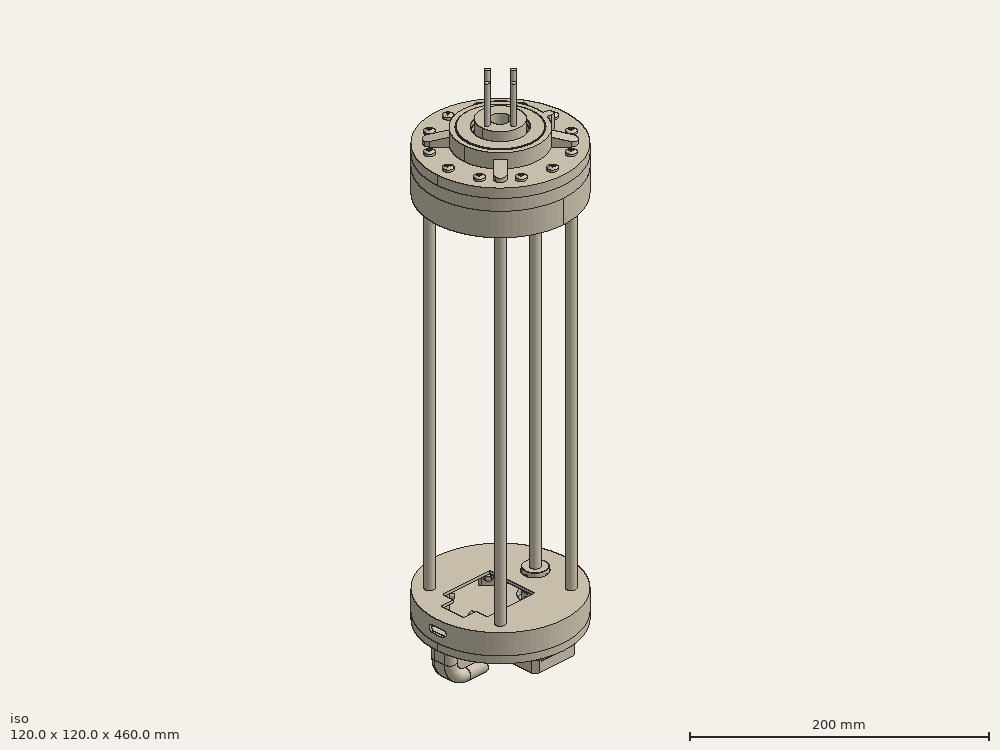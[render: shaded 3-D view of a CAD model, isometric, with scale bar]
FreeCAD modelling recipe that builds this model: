
FCSTD DOCUMENT  (FreeCAD 0.19R)
Label: Z-axis_a2p
License: All rights reserved
LicenseURL: http://en.wikipedia.org/wiki/All_rights_reserved
objects: Part::FeaturePython×103, App::FeaturePython×86, Spreadsheet::Sheet×2
note: 103 computed .brp shape members not serialized (recipe doc carries the construction recipe); baked Part::Feature solids carry a one-line shape summary decoded from their .brp

FEATURE [Part::FeaturePython] b_Z_axis_top_plate_001_  label="Z-axis_top_plate_001"  # a2plus imported part (geometry in sourceFile) (typed FeaturePython)
  a2p_Version = V0.1
  fixedPosition = true
  objectType = a2pPart
  sourceFile = ./Z-axis_top_plate.FCStd
  subassemblyImport = false
  timeLastImport = 1619853054
  updateColors = true
FEATURE [Part::FeaturePython] b_Clamp_smoth_rod_8mm_single_screw_001_  label="Clamp_smoth_rod_8mm_single_screw_001"  # a2plus imported part (geometry in sourceFile) (typed FeaturePython)
  Placement = pos=(-33.5876,-33.5876,13) rot=(0,0,1;0.785398rad)
  a2p_Version = V0.1
  fixedPosition = false
  objectType = a2pPart
  sourceFile = ./Clamp_smoth_rod_8mm_single_screw.FCStd
  subassemblyImport = false
  timeLastImport = 1.61989e+09
  updateColors = true
FEATURE [Part::FeaturePython] b_Clamp_smoth_rod_8mm_single_screw_001_001  label="Clamp_smoth_rod_8mm_single_screw_002"  # a2plus imported part (geometry in sourceFile) (typed FeaturePython)
  Placement = pos=(33.5876,33.5876,13) rot=(0,0,1;3.92699rad)
  a2p_Version = V0.1
  fixedPosition = false
  objectType = a2pPart
  sourceFile = ./Clamp_smoth_rod_8mm_single_screw.FCStd
  subassemblyImport = false
  timeLastImport = 1.61989e+09
  updateColors = true
FEATURE [Part::FeaturePython] b_Top_cover_8mm_001_  label="Top_cover_8mm_001"  # a2plus imported part (geometry in sourceFile) (typed FeaturePython)
  Placement = pos=(-1.16153e-07,1.92173e-07,24) rot=(0.707107,0.707107,0;3.14159rad)
  a2p_Version = V0.1
  fixedPosition = false
  objectType = a2pPart
  sourceFile = ./Top_cover_8mm.FCStd
  subassemblyImport = false
  timeLastImport = 1.62017e+09
  updateColors = true
FEATURE [App::FeaturePython] planeCoincident_003  label="planeCoincident_003__Z-axis_top_plate_001"  # a2plus constraint (typed FeaturePython)
  Object1 = b_Top_cover_8mm_001_
  Object2 = b_Z_axis_top_plate_001_
  ParentTreeObject = -> b_Top_cover_8mm_001_
  SubElement1 = Face11
  SubElement2 = Face1
  Suppressed = false
  Type = plane
  directionConstraint = 1
  offset = 0
FEATURE [App::FeaturePython] planeCoincident_003_mirror  label="planeCoincident_003__Top_cover_8mm_001"  # a2plus constraint (typed FeaturePython)
  Object1 = b_Top_cover_8mm_001_
  Object2 = b_Z_axis_top_plate_001_
  ParentTreeObject = -> b_Z_axis_top_plate_001_
  SubElement1 = Face11
  SubElement2 = Face1
  Suppressed = false
  Type = plane
  directionConstraint = 1
  offset = 0
FEATURE [App::FeaturePython] axisCoincident_005  label="axisCoincident_005__Z-axis_top_plate_001"  # a2plus constraint (typed FeaturePython)
  Object1 = b_Top_cover_8mm_001_
  Object2 = b_Z_axis_top_plate_001_
  ParentTreeObject = -> b_Top_cover_8mm_001_
  SubElement1 = Face16
  SubElement2 = Face11
  Suppressed = false
  Type = axial
  directionConstraint = 1
  lockRotation = false
FEATURE [App::FeaturePython] axisCoincident_005_mirror  label="axisCoincident_005__Top_cover_8mm_001"  # a2plus constraint (typed FeaturePython)
  Object1 = b_Top_cover_8mm_001_
  Object2 = b_Z_axis_top_plate_001_
  ParentTreeObject = -> b_Z_axis_top_plate_001_
  SubElement1 = Face16
  SubElement2 = Face11
  Suppressed = false
  Type = axial
  directionConstraint = 1
  lockRotation = false
FEATURE [App::FeaturePython] axisCoincident_001  label="axisCoincident_001__Z-axis_top_plate_001"  # a2plus constraint (typed FeaturePython)
  Object1 = b_Clamp_smoth_rod_8mm_single_screw_001_
  Object2 = b_Z_axis_top_plate_001_
  ParentTreeObject = -> b_Clamp_smoth_rod_8mm_single_screw_001_
  SubElement1 = Face67
  SubElement2 = Face29
  Suppressed = false
  Type = axial
  directionConstraint = 0
  lockRotation = false
FEATURE [App::FeaturePython] axisCoincident_001_mirror  label="axisCoincident_001__Clamp_smoth_rod_8mm_single_screw_001"  # a2plus constraint (typed FeaturePython)
  Object1 = b_Clamp_smoth_rod_8mm_single_screw_001_
  Object2 = b_Z_axis_top_plate_001_
  ParentTreeObject = -> b_Z_axis_top_plate_001_
  SubElement1 = Face67
  SubElement2 = Face29
  Suppressed = false
  Type = axial
  directionConstraint = 0
  lockRotation = false
FEATURE [App::FeaturePython] axisCoincident_002  label="axisCoincident_002__Clamp_smoth_rod_8mm_single_screw_001"  # a2plus constraint (typed FeaturePython)
  Object1 = b_Z_axis_top_plate_001_
  Object2 = b_Clamp_smoth_rod_8mm_single_screw_001_
  ParentTreeObject = -> b_Z_axis_top_plate_001_
  SubElement1 = Face31
  SubElement2 = Face66
  Suppressed = false
  Type = axial
  directionConstraint = 0
  lockRotation = false
FEATURE [App::FeaturePython] axisCoincident_002_mirror  label="axisCoincident_002__Z-axis_top_plate_001"  # a2plus constraint (typed FeaturePython)
  Object1 = b_Z_axis_top_plate_001_
  Object2 = b_Clamp_smoth_rod_8mm_single_screw_001_
  ParentTreeObject = -> b_Clamp_smoth_rod_8mm_single_screw_001_
  SubElement1 = Face31
  SubElement2 = Face66
  Suppressed = false
  Type = axial
  directionConstraint = 0
  lockRotation = false
FEATURE [App::FeaturePython] axisCoincident_003  label="axisCoincident_003__Clamp_smoth_rod_8mm_single_screw_002"  # a2plus constraint (typed FeaturePython)
  Object1 = b_Z_axis_top_plate_001_
  Object2 = b_Clamp_smoth_rod_8mm_single_screw_001_001
  ParentTreeObject = -> b_Z_axis_top_plate_001_
  SubElement1 = Face21
  SubElement2 = Face67
  Suppressed = false
  Type = axial
  directionConstraint = 0
  lockRotation = false
FEATURE [App::FeaturePython] axisCoincident_003_mirror  label="axisCoincident_003__Z-axis_top_plate_001"  # a2plus constraint (typed FeaturePython)
  Object1 = b_Z_axis_top_plate_001_
  Object2 = b_Clamp_smoth_rod_8mm_single_screw_001_001
  ParentTreeObject = -> b_Clamp_smoth_rod_8mm_single_screw_001_001
  SubElement1 = Face21
  SubElement2 = Face67
  Suppressed = false
  Type = axial
  directionConstraint = 0
  lockRotation = false
FEATURE [App::FeaturePython] axisCoincident_004  label="axisCoincident_004__Z-axis_top_plate_001"  # a2plus constraint (typed FeaturePython)
  Object1 = b_Clamp_smoth_rod_8mm_single_screw_001_001
  Object2 = b_Z_axis_top_plate_001_
  ParentTreeObject = -> b_Clamp_smoth_rod_8mm_single_screw_001_001
  SubElement1 = Face66
  SubElement2 = Face23
  Suppressed = false
  Type = axial
  directionConstraint = 0
  lockRotation = false
FEATURE [App::FeaturePython] axisCoincident_004_mirror  label="axisCoincident_004__Clamp_smoth_rod_8mm_single_screw_002"  # a2plus constraint (typed FeaturePython)
  Object1 = b_Clamp_smoth_rod_8mm_single_screw_001_001
  Object2 = b_Z_axis_top_plate_001_
  ParentTreeObject = -> b_Z_axis_top_plate_001_
  SubElement1 = Face66
  SubElement2 = Face23
  Suppressed = false
  Type = axial
  directionConstraint = 0
  lockRotation = false
FEATURE [Part::FeaturePython] b_Clamp_smoth_rod_8mm_single_screw_001_002  label="Clamp_smoth_rod_8mm_single_screw_003"  # a2plus imported part (geometry in sourceFile) (typed FeaturePython)
  Placement = pos=(33.5876,-33.5876,13) rot=(0.382683,0.92388,0;3.14159rad)
  a2p_Version = V0.1
  fixedPosition = false
  objectType = a2pPart
  sourceFile = ./Clamp_smoth_rod_8mm_single_screw.FCStd
  subassemblyImport = false
  timeLastImport = 1.61989e+09
  updateColors = true
FEATURE [Part::FeaturePython] b_Clamp_smoth_rod_8mm_single_screw_001_003  label="Clamp_smoth_rod_8mm_single_screw_004"  # a2plus imported part (geometry in sourceFile) (typed FeaturePython)
  Placement = pos=(-33.5876,33.5876,13) rot=(0.92388,-0.382683,0;3.14159rad)
  a2p_Version = V0.1
  fixedPosition = false
  objectType = a2pPart
  sourceFile = ./Clamp_smoth_rod_8mm_single_screw.FCStd
  subassemblyImport = false
  timeLastImport = 1.61989e+09
  updateColors = true
FEATURE [App::FeaturePython] planeCoincident_001  label="planeCoincident_001__Z-axis_top_plate_001"  # a2plus constraint (typed FeaturePython)
  Object1 = b_Clamp_smoth_rod_8mm_single_screw_001_003
  Object2 = b_Z_axis_top_plate_001_
  ParentTreeObject = -> b_Clamp_smoth_rod_8mm_single_screw_001_003
  SubElement1 = Face36
  SubElement2 = Face1
  Suppressed = false
  Type = plane
  directionConstraint = 1
  offset = 0
FEATURE [App::FeaturePython] planeCoincident_001_mirror  label="planeCoincident_001__Clamp_smoth_rod_8mm_single_screw_004"  # a2plus constraint (typed FeaturePython)
  Object1 = b_Clamp_smoth_rod_8mm_single_screw_001_003
  Object2 = b_Z_axis_top_plate_001_
  ParentTreeObject = -> b_Z_axis_top_plate_001_
  SubElement1 = Face36
  SubElement2 = Face1
  Suppressed = false
  Type = plane
  directionConstraint = 1
  offset = 0
FEATURE [App::FeaturePython] axisCoincident_007  label="axisCoincident_007__Z-axis_top_plate_001"  # a2plus constraint (typed FeaturePython)
  Object1 = b_Clamp_smoth_rod_8mm_single_screw_001_003
  Object2 = b_Z_axis_top_plate_001_
  ParentTreeObject = -> b_Clamp_smoth_rod_8mm_single_screw_001_003
  SubElement1 = Face67
  SubElement2 = Face27
  Suppressed = false
  Type = axial
  directionConstraint = 1
  lockRotation = false
FEATURE [App::FeaturePython] axisCoincident_007_mirror  label="axisCoincident_007__Clamp_smoth_rod_8mm_single_screw_004"  # a2plus constraint (typed FeaturePython)
  Object1 = b_Clamp_smoth_rod_8mm_single_screw_001_003
  Object2 = b_Z_axis_top_plate_001_
  ParentTreeObject = -> b_Z_axis_top_plate_001_
  SubElement1 = Face67
  SubElement2 = Face27
  Suppressed = false
  Type = axial
  directionConstraint = 1
  lockRotation = false
FEATURE [App::FeaturePython] axisCoincident_008  label="axisCoincident_008__Z-axis_top_plate_001"  # a2plus constraint (typed FeaturePython)
  Object1 = b_Clamp_smoth_rod_8mm_single_screw_001_003
  Object2 = b_Z_axis_top_plate_001_
  ParentTreeObject = -> b_Clamp_smoth_rod_8mm_single_screw_001_003
  SubElement1 = Face66
  SubElement2 = Face25
  Suppressed = false
  Type = axial
  directionConstraint = 1
  lockRotation = false
FEATURE [App::FeaturePython] axisCoincident_008_mirror  label="axisCoincident_008__Clamp_smoth_rod_8mm_single_screw_004"  # a2plus constraint (typed FeaturePython)
  Object1 = b_Clamp_smoth_rod_8mm_single_screw_001_003
  Object2 = b_Z_axis_top_plate_001_
  ParentTreeObject = -> b_Z_axis_top_plate_001_
  SubElement1 = Face66
  SubElement2 = Face25
  Suppressed = false
  Type = axial
  directionConstraint = 1
  lockRotation = false
FEATURE [App::FeaturePython] planeCoincident_002  label="planeCoincident_002__Clamp_smoth_rod_8mm_single_screw_003"  # a2plus constraint (typed FeaturePython)
  Object1 = b_Z_axis_top_plate_001_
  Object2 = b_Clamp_smoth_rod_8mm_single_screw_001_002
  ParentTreeObject = -> b_Z_axis_top_plate_001_
  SubElement1 = Face1
  SubElement2 = Face36
  Suppressed = false
  Type = plane
  directionConstraint = 1
  offset = 0
FEATURE [App::FeaturePython] planeCoincident_002_mirror  label="planeCoincident_002__Z-axis_top_plate_001"  # a2plus constraint (typed FeaturePython)
  Object1 = b_Z_axis_top_plate_001_
  Object2 = b_Clamp_smoth_rod_8mm_single_screw_001_002
  ParentTreeObject = -> b_Clamp_smoth_rod_8mm_single_screw_001_002
  SubElement1 = Face1
  SubElement2 = Face36
  Suppressed = false
  Type = plane
  directionConstraint = 1
  offset = 0
FEATURE [App::FeaturePython] axisCoincident_009  label="axisCoincident_009__Z-axis_top_plate_001"  # a2plus constraint (typed FeaturePython)
  Object1 = b_Clamp_smoth_rod_8mm_single_screw_001_002
  Object2 = b_Z_axis_top_plate_001_
  ParentTreeObject = -> b_Clamp_smoth_rod_8mm_single_screw_001_002
  SubElement1 = Face67
  SubElement2 = Face19
  Suppressed = false
  Type = axial
  directionConstraint = 1
  lockRotation = false
FEATURE [App::FeaturePython] axisCoincident_009_mirror  label="axisCoincident_009__Clamp_smoth_rod_8mm_single_screw_003"  # a2plus constraint (typed FeaturePython)
  Object1 = b_Clamp_smoth_rod_8mm_single_screw_001_002
  Object2 = b_Z_axis_top_plate_001_
  ParentTreeObject = -> b_Z_axis_top_plate_001_
  SubElement1 = Face67
  SubElement2 = Face19
  Suppressed = false
  Type = axial
  directionConstraint = 1
  lockRotation = false
FEATURE [App::FeaturePython] axisCoincident_010  label="axisCoincident_010__Z-axis_top_plate_001"  # a2plus constraint (typed FeaturePython)
  Object1 = b_Clamp_smoth_rod_8mm_single_screw_001_002
  Object2 = b_Z_axis_top_plate_001_
  ParentTreeObject = -> b_Clamp_smoth_rod_8mm_single_screw_001_002
  SubElement1 = Face66
  SubElement2 = Face33
  Suppressed = false
  Type = axial
  directionConstraint = 1
  lockRotation = false
FEATURE [App::FeaturePython] axisCoincident_010_mirror  label="axisCoincident_010__Clamp_smoth_rod_8mm_single_screw_003"  # a2plus constraint (typed FeaturePython)
  Object1 = b_Clamp_smoth_rod_8mm_single_screw_001_002
  Object2 = b_Z_axis_top_plate_001_
  ParentTreeObject = -> b_Z_axis_top_plate_001_
  SubElement1 = Face66
  SubElement2 = Face33
  Suppressed = false
  Type = axial
  directionConstraint = 1
  lockRotation = false
FEATURE [Part::FeaturePython] b_Z_axis_endstop_support_001_  label="Z-axis_endstop_support_001"  # a2plus imported part (geometry in sourceFile) (typed FeaturePython)
  Placement = pos=(-53,1.64821e-06,1.13151e-07) rot=(1,0,0;3.14159rad)
  a2p_Version = V0.1
  fixedPosition = false
  objectType = a2pPart
  sourceFile = ./Z-axis_endstop_support.FCStd
  subassemblyImport = false
  timeLastImport = 1.61989e+09
  updateColors = true
FEATURE [App::FeaturePython] planeCoincident_004  label="planeCoincident_004__Z-axis_top_plate_001"  # a2plus constraint (typed FeaturePython)
  Object1 = b_Z_axis_endstop_support_001_
  Object2 = b_Z_axis_top_plate_001_
  ParentTreeObject = -> b_Z_axis_endstop_support_001_
  SubElement1 = Face1
  SubElement2 = Face48
  Suppressed = false
  Type = plane
  directionConstraint = 0
  offset = 0
FEATURE [App::FeaturePython] planeCoincident_004_mirror  label="planeCoincident_004__Z-axis_endstop_support_001"  # a2plus constraint (typed FeaturePython)
  Object1 = b_Z_axis_endstop_support_001_
  Object2 = b_Z_axis_top_plate_001_
  ParentTreeObject = -> b_Z_axis_top_plate_001_
  SubElement1 = Face1
  SubElement2 = Face48
  Suppressed = false
  Type = plane
  directionConstraint = 0
  offset = 0
FEATURE [App::FeaturePython] axisCoincident_011  label="axisCoincident_011__Z-axis_top_plate_001"  # a2plus constraint (typed FeaturePython)
  Object1 = b_Z_axis_endstop_support_001_
  Object2 = b_Z_axis_top_plate_001_
  ParentTreeObject = -> b_Z_axis_endstop_support_001_
  SubElement1 = Face74
  SubElement2 = Face49
  Suppressed = false
  Type = axial
  directionConstraint = 1
  lockRotation = true
FEATURE [App::FeaturePython] axisCoincident_011_mirror  label="axisCoincident_011__Z-axis_endstop_support_001"  # a2plus constraint (typed FeaturePython)
  Object1 = b_Z_axis_endstop_support_001_
  Object2 = b_Z_axis_top_plate_001_
  ParentTreeObject = -> b_Z_axis_top_plate_001_
  SubElement1 = Face74
  SubElement2 = Face49
  Suppressed = false
  Type = axial
  directionConstraint = 1
  lockRotation = true
FEATURE [Part::FeaturePython] b_Stepper_NEMA_17____20mm_shaft1_001_  label="Stepper NEMA 17 -  20mm shaft1_001"  # a2plus imported part (geometry in sourceFile) (typed FeaturePython)
  Placement = pos=(24.5386,-37.2291,-61.0261) rot=(0,0,1;0rad)
  a2p_Version = V0.1
  fixedPosition = false
  muxInfo = <blob: 18848 chars omitted>
  objectType = a2pPart
  sourceFile = ./Stepper NEMA 17 -  20mm shaft.step
  subassemblyImport = false
  timeLastImport = 1598802185
  updateColors = true
FEATURE [App::FeaturePython] circularEdge_001  label="circularEdge_001__Z-axis_top_plate_001"  # a2plus constraint (typed FeaturePython)
  Object1 = b_Stepper_NEMA_17____20mm_shaft1_001_
  Object2 = b_Z_axis_top_plate_001_
  ParentTreeObject = -> b_Stepper_NEMA_17____20mm_shaft1_001_
  SubElement1 = Edge25
  SubElement2 = Edge132
  Suppressed = false
  Type = circularEdge
  directionConstraint = 0
  lockRotation = true
  offset = 0
FEATURE [App::FeaturePython] circularEdge_001_mirror  label="circularEdge_001__Stepper NEMA 17 -  20mm shaft1_001"  # a2plus constraint (typed FeaturePython)
  Object1 = b_Stepper_NEMA_17____20mm_shaft1_001_
  Object2 = b_Z_axis_top_plate_001_
  ParentTreeObject = -> b_Z_axis_top_plate_001_
  SubElement1 = Edge25
  SubElement2 = Edge132
  Suppressed = false
  Type = circularEdge
  directionConstraint = 0
  lockRotation = true
  offset = 0
FEATURE [Part::FeaturePython] b_Micro_switch1_001_  label="Micro switch1_001"  # a2plus imported part (geometry in sourceFile) (typed FeaturePython)
  Placement = pos=(-35.8,3,0.6) rot=(1,0,0;1.5708rad)
  a2p_Version = V0.1
  fixedPosition = false
  muxInfo = <blob: 6853 chars omitted>
  objectType = a2pPart
  sourceFile = ./Micro switch.step
  subassemblyImport = false
  timeLastImport = 1598970250
  updateColors = true
FEATURE [Part::FeaturePython] b_pin_3mmx10mm_001_  label="pin_3mmx10mm_001"  # a2plus imported part (geometry in sourceFile) (typed FeaturePython)
  Placement = pos=(-30.8,1.00232e-07,-1.9) rot=(0.18533,0,-0.982676;0rad)
  a2p_Version = V0.1
  fixedPosition = false
  muxInfo = [VERTEXES] | V;Pad;1;2; | V;Pad;2;2; | [EDGES] | E;Pad;1;3; | E;Pad;2;3; | E;Pad;3;3; | [FACES] | F;Pad;1;3; | F;Pad;2;3; | F;Pad;3;3;
  objectType = a2pPart
  sourceFile = ./pin_3mmx10mm.FCStd
  subassemblyImport = false
  timeLastImport = 1.61984e+09
  updateColors = true
FEATURE [App::FeaturePython] axisCoincident_012  label="axisCoincident_012__pin_3mmx10mm_001"  # a2plus constraint (typed FeaturePython)
  Object1 = b_Micro_switch1_001_
  Object2 = b_pin_3mmx10mm_001_
  ParentTreeObject = -> b_Micro_switch1_001_
  SubElement1 = Face10
  SubElement2 = Face1
  Suppressed = false
  Type = axial
  directionConstraint = 1
  lockRotation = false
FEATURE [App::FeaturePython] axisCoincident_012_mirror  label="axisCoincident_012__Micro switch1_001"  # a2plus constraint (typed FeaturePython)
  Object1 = b_Micro_switch1_001_
  Object2 = b_pin_3mmx10mm_001_
  ParentTreeObject = -> b_pin_3mmx10mm_001_
  SubElement1 = Face10
  SubElement2 = Face1
  Suppressed = false
  Type = axial
  directionConstraint = 1
  lockRotation = false
FEATURE [App::FeaturePython] planeCoincident_005  label="planeCoincident_005__Micro switch1_001"  # a2plus constraint (typed FeaturePython)
  Object1 = b_pin_3mmx10mm_001_
  Object2 = b_Micro_switch1_001_
  ParentTreeObject = -> b_pin_3mmx10mm_001_
  SubElement1 = Face3
  SubElement2 = Face8
  Suppressed = false
  Type = plane
  directionConstraint = 1
  offset = 2
FEATURE [App::FeaturePython] planeCoincident_005_mirror  label="planeCoincident_005__pin_3mmx10mm_001"  # a2plus constraint (typed FeaturePython)
  Object1 = b_pin_3mmx10mm_001_
  Object2 = b_Micro_switch1_001_
  ParentTreeObject = -> b_Micro_switch1_001_
  SubElement1 = Face3
  SubElement2 = Face8
  Suppressed = false
  Type = plane
  directionConstraint = 1
  offset = 2
FEATURE [App::FeaturePython] axisCoincident_013  label="axisCoincident_013__pin_3mmx10mm_001"  # a2plus constraint (typed FeaturePython)
  Object1 = b_Z_axis_endstop_support_001_
  Object2 = b_pin_3mmx10mm_001_
  ParentTreeObject = -> b_Z_axis_endstop_support_001_
  SubElement1 = Face57
  SubElement2 = Face1
  Suppressed = false
  Type = axial
  directionConstraint = 0
  lockRotation = false
FEATURE [App::FeaturePython] axisCoincident_013_mirror  label="axisCoincident_013__Z-axis_endstop_support_001"  # a2plus constraint (typed FeaturePython)
  Object1 = b_Z_axis_endstop_support_001_
  Object2 = b_pin_3mmx10mm_001_
  ParentTreeObject = -> b_pin_3mmx10mm_001_
  SubElement1 = Face57
  SubElement2 = Face1
  Suppressed = false
  Type = axial
  directionConstraint = 0
  lockRotation = false
FEATURE [App::FeaturePython] planeCoincident_006  label="planeCoincident_006__Z-axis_endstop_support_001"  # a2plus constraint (typed FeaturePython)
  Object1 = b_pin_3mmx10mm_001_
  Object2 = b_Z_axis_endstop_support_001_
  ParentTreeObject = -> b_pin_3mmx10mm_001_
  SubElement1 = Face3
  SubElement2 = Face73
  Suppressed = false
  Type = plane
  directionConstraint = 1
  offset = 0
FEATURE [App::FeaturePython] planeCoincident_006_mirror  label="planeCoincident_006__pin_3mmx10mm_001"  # a2plus constraint (typed FeaturePython)
  Object1 = b_pin_3mmx10mm_001_
  Object2 = b_Z_axis_endstop_support_001_
  ParentTreeObject = -> b_Z_axis_endstop_support_001_
  SubElement1 = Face3
  SubElement2 = Face73
  Suppressed = false
  Type = plane
  directionConstraint = 1
  offset = 0
FEATURE [Part::FeaturePython] b_pin_3mmx10mm_001_001  label="pin_3mmx10mm_002"  # a2plus imported part (geometry in sourceFile) (typed FeaturePython)
  Placement = pos=(-40.3,7.4028e-07,-1.9) rot=(0.15264,0,-0.988282;0rad)
  a2p_Version = V0.1
  fixedPosition = false
  muxInfo = [VERTEXES] | V;Pad;1;2; | V;Pad;2;2; | [EDGES] | E;Pad;1;3; | E;Pad;2;3; | E;Pad;3;3; | [FACES] | F;Pad;1;3; | F;Pad;2;3; | F;Pad;3;3;
  objectType = a2pPart
  sourceFile = ./pin_3mmx10mm.FCStd
  subassemblyImport = false
  timeLastImport = 1.61984e+09
  updateColors = true
FEATURE [App::FeaturePython] axisCoincident_014  label="axisCoincident_014__pin_3mmx10mm_002"  # a2plus constraint (typed FeaturePython)
  Object1 = b_Micro_switch1_001_
  Object2 = b_pin_3mmx10mm_001_001
  ParentTreeObject = -> b_Micro_switch1_001_
  SubElement1 = Face9
  SubElement2 = Face1
  Suppressed = false
  Type = axial
  directionConstraint = 1
  lockRotation = false
FEATURE [App::FeaturePython] axisCoincident_014_mirror  label="axisCoincident_014__Micro switch1_001"  # a2plus constraint (typed FeaturePython)
  Object1 = b_Micro_switch1_001_
  Object2 = b_pin_3mmx10mm_001_001
  ParentTreeObject = -> b_pin_3mmx10mm_001_001
  SubElement1 = Face9
  SubElement2 = Face1
  Suppressed = false
  Type = axial
  directionConstraint = 1
  lockRotation = false
FEATURE [App::FeaturePython] planeCoincident_007  label="planeCoincident_007__pin_3mmx10mm_001"  # a2plus constraint (typed FeaturePython)
  Object1 = b_pin_3mmx10mm_001_001
  Object2 = b_pin_3mmx10mm_001_
  ParentTreeObject = -> b_pin_3mmx10mm_001_001
  SubElement1 = Face3
  SubElement2 = Face3
  Suppressed = false
  Type = plane
  directionConstraint = 0
  offset = 0
FEATURE [App::FeaturePython] planeCoincident_007_mirror  label="planeCoincident_007__pin_3mmx10mm_002"  # a2plus constraint (typed FeaturePython)
  Object1 = b_pin_3mmx10mm_001_001
  Object2 = b_pin_3mmx10mm_001_
  ParentTreeObject = -> b_pin_3mmx10mm_001_
  SubElement1 = Face3
  SubElement2 = Face3
  Suppressed = false
  Type = plane
  directionConstraint = 0
  offset = 0
FEATURE [Part::FeaturePython] b_TR8_lead_screw_300mm_001_  label="TR8_lead_screw_300mm_001"  # a2plus imported part (geometry in sourceFile) (typed FeaturePython)
  Placement = pos=(33,1.0072e-08,20) rot=(0.000129,-0.000114,1;9.8e-05rad)
  a2p_Version = V0.1
  fixedPosition = false
  muxInfo = [VERTEXES] | V;Pad;1;2; | V;Pad;2;2; | [EDGES] | E;Pad;1;3; | E;Pad;2;3; | E;Pad;3;3; | [FACES] | F;Pad;1;3; | F;Pad;2;3; | F;Pad;3;3;
  objectType = a2pPart
  sourceFile = ./TR8_lead_screw_300mm.FCStd
  subassemblyImport = false
  timeLastImport = 1.61984e+09
  updateColors = true
FEATURE [App::FeaturePython] circularEdge_002  label="circularEdge_002__Stepper NEMA 17 -  20mm shaft1_001"  # a2plus constraint (typed FeaturePython)
  Object1 = b_TR8_lead_screw_300mm_001_
  Object2 = b_Stepper_NEMA_17____20mm_shaft1_001_
  ParentTreeObject = -> b_TR8_lead_screw_300mm_001_
  SubElement1 = Edge2
  SubElement2 = Edge23
  Suppressed = false
  Type = circularEdge
  directionConstraint = 0
  lockRotation = false
  offset = 0
FEATURE [App::FeaturePython] circularEdge_002_mirror  label="circularEdge_002__TR8_lead_screw_300mm_001"  # a2plus constraint (typed FeaturePython)
  Object1 = b_TR8_lead_screw_300mm_001_
  Object2 = b_Stepper_NEMA_17____20mm_shaft1_001_
  ParentTreeObject = -> b_Stepper_NEMA_17____20mm_shaft1_001_
  SubElement1 = Edge2
  SubElement2 = Edge23
  Suppressed = false
  Type = circularEdge
  directionConstraint = 0
  lockRotation = false
  offset = 0
FEATURE [Part::FeaturePython] b_Z_axis_bottom_plate_001_  label="Z-axis_bottom_plate_001"  # a2plus imported part (geometry in sourceFile) (typed FeaturePython)
  Placement = pos=(2.49245e-05,-2.45911e-05,360) rot=(1,0,0;3.14159rad)
  a2p_Version = V0.1
  fixedPosition = false
  objectType = a2pPart
  sourceFile = ./Z-axis_bottom_plate.FCStd
  subassemblyImport = false
  timeLastImport = 1.62009e+09
  updateColors = true
FEATURE [Part::FeaturePython] b_Bearing_608_spacer_001_  label="Bearing_608_spacer_001"  # a2plus imported part (geometry in sourceFile) (typed FeaturePython)
  Placement = pos=(33,5.21436e-06,350) rot=(0.866026,-0.5,0;3.14159rad)
  a2p_Version = V0.1
  fixedPosition = false
  objectType = a2pPart
  sourceFile = ./Bearing_608_spacer.FCStd
  subassemblyImport = false
  timeLastImport = 1.61989e+09
  updateColors = true
FEATURE [Part::FeaturePython] b_Ball_bearing_6081_001_  label="Ball_bearing_6081_001"  # a2plus imported part (geometry in sourceFile) (typed FeaturePython)
  Placement = pos=(33,5.96645e-06,310.01) rot=(1,0,0;1.5708rad)
  a2p_Version = V0.1
  fixedPosition = false
  muxInfo = <blob: 2406 chars omitted>
  objectType = a2pPart
  sourceFile = ./Ball_bearing_608.step
  subassemblyImport = false
  timeLastImport = 1.61984e+09
  updateColors = true
FEATURE [Part::FeaturePython] b_J1_coupler_8mm1_001_  label="J1_coupler_8mm1_001"  # a2plus imported part (geometry in sourceFile) (typed FeaturePython)
  Placement = pos=(2.49949e-05,-2.50329e-05,368) rot=(0.57735,0.57735,-0.57735;4.18879rad)
  a2p_Version = V0.1
  fixedPosition = false
  muxInfo = <blob: 10829 chars omitted>
  objectType = a2pPart
  sourceFile = ./J1_coupler_8mm.step
  subassemblyImport = false
  timeLastImport = 1.61984e+09
  updateColors = true
FEATURE [Part::FeaturePython] b_Clamp_smoth_rod_8mm_single_screw_001_004  label="Clamp_smoth_rod_8mm_single_screw_005"  # a2plus imported part (geometry in sourceFile) (typed FeaturePython)
  Placement = pos=(33.5876,33.5876,343) rot=(0,0,1;3.92699rad)
  a2p_Version = V0.1
  fixedPosition = false
  objectType = a2pPart
  sourceFile = ./Clamp_smoth_rod_8mm_single_screw.FCStd
  subassemblyImport = false
  timeLastImport = 1.61989e+09
  updateColors = true
FEATURE [Part::FeaturePython] b_Clamp_smoth_rod_8mm_single_screw_001_005  label="Clamp_smoth_rod_8mm_single_screw_006"  # a2plus imported part (geometry in sourceFile) (typed FeaturePython)
  Placement = pos=(33.5876,-33.5876,343) rot=(0.382683,0.92388,0;3.14159rad)
  a2p_Version = V0.1
  fixedPosition = false
  objectType = a2pPart
  sourceFile = ./Clamp_smoth_rod_8mm_single_screw.FCStd
  subassemblyImport = false
  timeLastImport = 1.61989e+09
  updateColors = true
FEATURE [Part::FeaturePython] b_Clamp_smoth_rod_8mm_single_screw_001_006  label="Clamp_smoth_rod_8mm_single_screw_007"  # a2plus imported part (geometry in sourceFile) (typed FeaturePython)
  Placement = pos=(-33.5875,-33.5876,343) rot=(0,0,1;0.785398rad)
  a2p_Version = V0.1
  fixedPosition = false
  objectType = a2pPart
  sourceFile = ./Clamp_smoth_rod_8mm_single_screw.FCStd
  subassemblyImport = false
  timeLastImport = 1.61989e+09
  updateColors = true
FEATURE [Part::FeaturePython] b_Clamp_smoth_rod_8mm_single_screw_001_007  label="Clamp_smoth_rod_8mm_single_screw_008"  # a2plus imported part (geometry in sourceFile) (typed FeaturePython)
  Placement = pos=(-33.5876,33.5875,343) rot=(0.92388,-0.382683,0;3.14159rad)
  a2p_Version = V0.1
  fixedPosition = false
  objectType = a2pPart
  sourceFile = ./Clamp_smoth_rod_8mm_single_screw.FCStd
  subassemblyImport = false
  timeLastImport = 1.61989e+09
  updateColors = true
FEATURE [Part::FeaturePython] b_Base_cover_8mm_001_  label="Base_cover_8mm_001"  # a2plus imported part (geometry in sourceFile) (typed FeaturePython)
  Placement = pos=(2.46476e-05,-2.35668e-05,329.5) rot=(1,0,0;1.5708rad)
  a2p_Version = V0.1
  fixedPosition = false
  objectType = a2pPart
  sourceFile = ./Base_cover_8mm.FCStd
  subassemblyImport = false
  timeLastImport = 1.61989e+09
  updateColors = true
FEATURE [App::FeaturePython] circularEdge_007  label="circularEdge_007__Bearing_608_spacer_001"  # a2plus constraint (typed FeaturePython)
  Object1 = b_Ball_bearing_6081_001_
  Object2 = b_Bearing_608_spacer_001_
  ParentTreeObject = -> b_Ball_bearing_6081_001_
  SubElement1 = Edge13
  SubElement2 = Edge84
  Suppressed = false
  Type = circularEdge
  directionConstraint = 0
  lockRotation = false
  offset = 0
FEATURE [App::FeaturePython] circularEdge_007_mirror  label="circularEdge_007__Ball_bearing_6081_001"  # a2plus constraint (typed FeaturePython)
  Object1 = b_Ball_bearing_6081_001_
  Object2 = b_Bearing_608_spacer_001_
  ParentTreeObject = -> b_Bearing_608_spacer_001_
  SubElement1 = Edge13
  SubElement2 = Edge84
  Suppressed = false
  Type = circularEdge
  directionConstraint = 0
  lockRotation = false
  offset = 0
FEATURE [Part::FeaturePython] b_Smooth_rod_8mm_360mm_001_  label="Smooth_rod_8mm_360mm_001"  # a2plus imported part (geometry in sourceFile) (typed FeaturePython)
  Placement = pos=(33.5876,33.5876,6) rot=(0,0,1;0rad)
  a2p_Version = V0.1
  fixedPosition = false
  muxInfo = [VERTEXES] | V;Pad;1;2; | V;Pad;2;2; | [EDGES] | E;Pad;1;3; | E;Pad;2;3; | E;Pad;3;3; | [FACES] | F;Pad;1;3; | F;Pad;2;3; | F;Pad;3;3;
  objectType = a2pPart
  sourceFile = ./Smooth_rod_8mm_360mm.FCStd
  subassemblyImport = false
  timeLastImport = 1.61985e+09
  updateColors = true
FEATURE [App::FeaturePython] circularEdge_003  label="circularEdge_003__Clamp_smoth_rod_8mm_single_screw_002"  # a2plus constraint (typed FeaturePython)
  Object1 = b_Smooth_rod_8mm_360mm_001_
  Object2 = b_Clamp_smoth_rod_8mm_single_screw_001_001
  ParentTreeObject = -> b_Smooth_rod_8mm_360mm_001_
  SubElement1 = Edge2
  SubElement2 = Edge4
  Suppressed = false
  Type = circularEdge
  directionConstraint = 0
  lockRotation = false
  offset = 0
FEATURE [App::FeaturePython] circularEdge_003_mirror  label="circularEdge_003__Smooth_rod_8mm_360mm_001"  # a2plus constraint (typed FeaturePython)
  Object1 = b_Smooth_rod_8mm_360mm_001_
  Object2 = b_Clamp_smoth_rod_8mm_single_screw_001_001
  ParentTreeObject = -> b_Clamp_smoth_rod_8mm_single_screw_001_001
  SubElement1 = Edge2
  SubElement2 = Edge4
  Suppressed = false
  Type = circularEdge
  directionConstraint = 0
  lockRotation = false
  offset = 0
FEATURE [App::FeaturePython] circularEdge_004  label="circularEdge_004__J1_coupler_8mm1_001"  # a2plus constraint (typed FeaturePython)
  Object1 = b_Smooth_rod_8mm_360mm_001_
  Object2 = b_J1_coupler_8mm1_001_
  ParentTreeObject = -> b_Smooth_rod_8mm_360mm_001_
  SubElement1 = Edge3
  SubElement2 = Edge143
  Suppressed = false
  Type = circularEdge
  directionConstraint = 1
  lockRotation = false
  offset = 0
FEATURE [App::FeaturePython] circularEdge_004_mirror  label="circularEdge_004__Smooth_rod_8mm_360mm_001"  # a2plus constraint (typed FeaturePython)
  Object1 = b_Smooth_rod_8mm_360mm_001_
  Object2 = b_J1_coupler_8mm1_001_
  ParentTreeObject = -> b_J1_coupler_8mm1_001_
  SubElement1 = Edge3
  SubElement2 = Edge143
  Suppressed = false
  Type = circularEdge
  directionConstraint = 1
  lockRotation = false
  offset = 0
FEATURE [Part::FeaturePython] b_Smooth_rod_8mm_360mm_001_001  label="Smooth_rod_8mm_360mm_002"  # a2plus imported part (geometry in sourceFile) (typed FeaturePython)
  Placement = pos=(-33.5876,33.5875,6) rot=(0.998487,0.054979,0;0rad)
  a2p_Version = V0.1
  fixedPosition = false
  muxInfo = [VERTEXES] | V;Pad;1;2; | V;Pad;2;2; | [EDGES] | E;Pad;1;3; | E;Pad;2;3; | E;Pad;3;3; | [FACES] | F;Pad;1;3; | F;Pad;2;3; | F;Pad;3;3;
  objectType = a2pPart
  sourceFile = ./Smooth_rod_8mm_360mm.FCStd
  subassemblyImport = false
  timeLastImport = 1.61985e+09
  updateColors = true
FEATURE [Part::FeaturePython] b_Smooth_rod_8mm_360mm_001_002  label="Smooth_rod_8mm_360mm_003"  # a2plus imported part (geometry in sourceFile) (typed FeaturePython)
  Placement = pos=(-33.5875,-33.5876,6) rot=(0.997723,0.067442,0;0rad)
  a2p_Version = V0.1
  fixedPosition = false
  muxInfo = [VERTEXES] | V;Pad;1;2; | V;Pad;2;2; | [EDGES] | E;Pad;1;3; | E;Pad;2;3; | E;Pad;3;3; | [FACES] | F;Pad;1;3; | F;Pad;2;3; | F;Pad;3;3;
  objectType = a2pPart
  sourceFile = ./Smooth_rod_8mm_360mm.FCStd
  subassemblyImport = false
  timeLastImport = 1.61985e+09
  updateColors = true
FEATURE [Part::FeaturePython] b_Smooth_rod_8mm_360mm_001_003  label="Smooth_rod_8mm_360mm_004"  # a2plus imported part (geometry in sourceFile) (typed FeaturePython)
  Placement = pos=(33.5876,-33.5876,6) rot=(0.997723,0.067442,0;0rad)
  a2p_Version = V0.1
  fixedPosition = false
  muxInfo = [VERTEXES] | V;Pad;1;2; | V;Pad;2;2; | [EDGES] | E;Pad;1;3; | E;Pad;2;3; | E;Pad;3;3; | [FACES] | F;Pad;1;3; | F;Pad;2;3; | F;Pad;3;3;
  objectType = a2pPart
  sourceFile = ./Smooth_rod_8mm_360mm.FCStd
  subassemblyImport = false
  timeLastImport = 1.61985e+09
  updateColors = true
FEATURE [App::FeaturePython] circularEdge_005  label="circularEdge_005__J1_coupler_8mm1_001"  # a2plus constraint (typed FeaturePython)
  Object1 = b_Smooth_rod_8mm_360mm_001_001
  Object2 = b_J1_coupler_8mm1_001_
  ParentTreeObject = -> b_Smooth_rod_8mm_360mm_001_001
  SubElement1 = Edge3
  SubElement2 = Edge139
  Suppressed = false
  Type = circularEdge
  directionConstraint = 1
  lockRotation = false
  offset = 0
FEATURE [App::FeaturePython] circularEdge_005_mirror  label="circularEdge_005__Smooth_rod_8mm_360mm_002"  # a2plus constraint (typed FeaturePython)
  Object1 = b_Smooth_rod_8mm_360mm_001_001
  Object2 = b_J1_coupler_8mm1_001_
  ParentTreeObject = -> b_J1_coupler_8mm1_001_
  SubElement1 = Edge3
  SubElement2 = Edge139
  Suppressed = false
  Type = circularEdge
  directionConstraint = 1
  lockRotation = false
  offset = 0
FEATURE [App::FeaturePython] circularEdge_006  label="circularEdge_006__J1_coupler_8mm1_001"  # a2plus constraint (typed FeaturePython)
  Object1 = b_Smooth_rod_8mm_360mm_001_003
  Object2 = b_J1_coupler_8mm1_001_
  ParentTreeObject = -> b_Smooth_rod_8mm_360mm_001_003
  SubElement1 = Edge3
  SubElement2 = Edge131
  Suppressed = false
  Type = circularEdge
  directionConstraint = 1
  lockRotation = false
  offset = 0
FEATURE [App::FeaturePython] circularEdge_006_mirror  label="circularEdge_006__Smooth_rod_8mm_360mm_004"  # a2plus constraint (typed FeaturePython)
  Object1 = b_Smooth_rod_8mm_360mm_001_003
  Object2 = b_J1_coupler_8mm1_001_
  ParentTreeObject = -> b_J1_coupler_8mm1_001_
  SubElement1 = Edge3
  SubElement2 = Edge131
  Suppressed = false
  Type = circularEdge
  directionConstraint = 1
  lockRotation = false
  offset = 0
FEATURE [App::FeaturePython] circularEdge_009  label="circularEdge_009__J1_coupler_8mm1_001"  # a2plus constraint (typed FeaturePython)
  Object1 = b_Smooth_rod_8mm_360mm_001_002
  Object2 = b_J1_coupler_8mm1_001_
  ParentTreeObject = -> b_Smooth_rod_8mm_360mm_001_002
  SubElement1 = Edge3
  SubElement2 = Edge135
  Suppressed = false
  Type = circularEdge
  directionConstraint = 1
  lockRotation = false
  offset = 0
FEATURE [App::FeaturePython] circularEdge_009_mirror  label="circularEdge_009__Smooth_rod_8mm_360mm_003"  # a2plus constraint (typed FeaturePython)
  Object1 = b_Smooth_rod_8mm_360mm_001_002
  Object2 = b_J1_coupler_8mm1_001_
  ParentTreeObject = -> b_J1_coupler_8mm1_001_
  SubElement1 = Edge3
  SubElement2 = Edge135
  Suppressed = false
  Type = circularEdge
  directionConstraint = 1
  lockRotation = false
  offset = 0
FEATURE [App::FeaturePython] planeCoincident_012  label="planeCoincident_012__Clamp_smoth_rod_8mm_single_screw_005"  # a2plus constraint (typed FeaturePython)
  Object1 = b_Clamp_smoth_rod_8mm_single_screw_001_007
  Object2 = b_Clamp_smoth_rod_8mm_single_screw_001_004
  ParentTreeObject = -> b_Clamp_smoth_rod_8mm_single_screw_001_007
  SubElement1 = Face36
  SubElement2 = Face1
  Suppressed = false
  Type = plane
  directionConstraint = 1
  offset = 0
FEATURE [App::FeaturePython] planeCoincident_012_mirror  label="planeCoincident_012__Clamp_smoth_rod_8mm_single_screw_008"  # a2plus constraint (typed FeaturePython)
  Object1 = b_Clamp_smoth_rod_8mm_single_screw_001_007
  Object2 = b_Clamp_smoth_rod_8mm_single_screw_001_004
  ParentTreeObject = -> b_Clamp_smoth_rod_8mm_single_screw_001_004
  SubElement1 = Face36
  SubElement2 = Face1
  Suppressed = false
  Type = plane
  directionConstraint = 1
  offset = 0
FEATURE [App::FeaturePython] planeCoincident_013  label="planeCoincident_013__Clamp_smoth_rod_8mm_single_screw_007"  # a2plus constraint (typed FeaturePython)
  Object1 = b_Clamp_smoth_rod_8mm_single_screw_001_007
  Object2 = b_Clamp_smoth_rod_8mm_single_screw_001_006
  ParentTreeObject = -> b_Clamp_smoth_rod_8mm_single_screw_001_007
  SubElement1 = Face36
  SubElement2 = Face1
  Suppressed = false
  Type = plane
  directionConstraint = 1
  offset = 0
FEATURE [App::FeaturePython] planeCoincident_013_mirror  label="planeCoincident_013__Clamp_smoth_rod_8mm_single_screw_008"  # a2plus constraint (typed FeaturePython)
  Object1 = b_Clamp_smoth_rod_8mm_single_screw_001_007
  Object2 = b_Clamp_smoth_rod_8mm_single_screw_001_006
  ParentTreeObject = -> b_Clamp_smoth_rod_8mm_single_screw_001_006
  SubElement1 = Face36
  SubElement2 = Face1
  Suppressed = false
  Type = plane
  directionConstraint = 1
  offset = 0
FEATURE [App::FeaturePython] planeCoincident_014  label="planeCoincident_014__Clamp_smoth_rod_8mm_single_screw_006"  # a2plus constraint (typed FeaturePython)
  Object1 = b_Clamp_smoth_rod_8mm_single_screw_001_007
  Object2 = b_Clamp_smoth_rod_8mm_single_screw_001_005
  ParentTreeObject = -> b_Clamp_smoth_rod_8mm_single_screw_001_007
  SubElement1 = Face36
  SubElement2 = Face36
  Suppressed = false
  Type = plane
  directionConstraint = 0
  offset = 0
FEATURE [App::FeaturePython] planeCoincident_014_mirror  label="planeCoincident_014__Clamp_smoth_rod_8mm_single_screw_008"  # a2plus constraint (typed FeaturePython)
  Object1 = b_Clamp_smoth_rod_8mm_single_screw_001_007
  Object2 = b_Clamp_smoth_rod_8mm_single_screw_001_005
  ParentTreeObject = -> b_Clamp_smoth_rod_8mm_single_screw_001_005
  SubElement1 = Face36
  SubElement2 = Face36
  Suppressed = false
  Type = plane
  directionConstraint = 0
  offset = 0
FEATURE [Part::FeaturePython] Nut  label="M4-Nut"  # Fasteners workbench fastener (typed FeaturePython)
  Placement = pos=(-43.487,-23.6881,340) rot=(0.960102,0.27965,0;3.14159rad)
  baseObject = -> b_Clamp_smoth_rod_8mm_single_screw_001_006 [Edge143]
  diameter = 6
  invert = false
  matchOuter = false
  offset = 0
  thread = false
  type = 7
FEATURE [Part::FeaturePython] Nut001  label="M4-Nut057"  # Fasteners workbench fastener (typed FeaturePython)
  Placement = pos=(-23.688,-43.4871,340) rot=(0.960102,0.27965,0;3.14159rad)
  baseObject = -> b_Clamp_smoth_rod_8mm_single_screw_001_006 [Edge142]
  diameter = 6
  invert = false
  matchOuter = false
  offset = 0
  thread = false
  type = 7
FEATURE [Part::FeaturePython] Nut002  label="M4-Nut069"  # Fasteners workbench fastener (typed FeaturePython)
  Placement = pos=(-20.8596,-32.1734,343) rot=(-0.707106,0.707107,0;1.5708rad)
  baseObject = -> b_Clamp_smoth_rod_8mm_single_screw_001_006 [Edge126]
  diameter = 6
  invert = false
  matchOuter = false
  offset = 0
  thread = false
  type = 7
FEATURE [Part::FeaturePython] Nut003  label="M4-Nut065"  # Fasteners workbench fastener (typed FeaturePython)
  Placement = pos=(23.6881,43.4871,340) rot=(0.965886,0.258966,0;3.14159rad)
  baseObject = -> b_Clamp_smoth_rod_8mm_single_screw_001_004 [Edge142]
  diameter = 6
  invert = false
  matchOuter = false
  offset = 0
  thread = false
  type = 7
FEATURE [Part::FeaturePython] Nut004  label="M4-Nut064"  # Fasteners workbench fastener (typed FeaturePython)
  Placement = pos=(43.4871,23.6881,340) rot=(0.965886,0.258966,0;3.14159rad)
  baseObject = -> b_Clamp_smoth_rod_8mm_single_screw_001_004 [Edge143]
  diameter = 6
  invert = false
  matchOuter = false
  offset = 0
  thread = false
  type = 7
FEATURE [Part::FeaturePython] Nut005  label="M4-Nut070"  # Fasteners workbench fastener (typed FeaturePython)
  Placement = pos=(20.8596,32.1734,343) rot=(0.707107,-0.707107,0;1.5708rad)
  baseObject = -> b_Clamp_smoth_rod_8mm_single_screw_001_004 [Edge126]
  diameter = 6
  invert = false
  matchOuter = false
  offset = 0
  thread = false
  type = 7
FEATURE [Part::FeaturePython] Nut006  label="M4-Nut013"  # Fasteners workbench fastener (typed FeaturePython)
  Placement = pos=(-43.4871,-23.6881,16) rot=(0,0,1;0rad)
  baseObject = -> b_Clamp_smoth_rod_8mm_single_screw_001_ [Edge169]
  diameter = 6
  invert = true
  matchOuter = false
  offset = 0
  thread = false
  type = 7
FEATURE [Part::FeaturePython] Nut007  label="M4-Nut012"  # Fasteners workbench fastener (typed FeaturePython)
  Placement = pos=(-23.6881,-43.4871,16) rot=(0,0,1;0rad)
  baseObject = -> b_Clamp_smoth_rod_8mm_single_screw_001_ [Edge168]
  diameter = 6
  invert = true
  matchOuter = false
  offset = 0
  thread = false
  type = 7
FEATURE [Part::FeaturePython] Nut008  label="M4-Nut008"  # Fasteners workbench fastener (typed FeaturePython)
  Placement = pos=(-20.8597,-32.1734,13) rot=(-0.707107,0.707107,0;1.5708rad)
  baseObject = -> b_Clamp_smoth_rod_8mm_single_screw_001_ [Edge126]
  diameter = 6
  invert = false
  matchOuter = false
  offset = 0
  thread = false
  type = 7
FEATURE [Part::FeaturePython] Nut009  label="M4-Nut009"  # Fasteners workbench fastener (typed FeaturePython)
  Placement = pos=(43.4871,-23.6881,16) rot=(0,0,1;0rad)
  baseObject = -> b_Clamp_smoth_rod_8mm_single_screw_001_002 [Edge143]
  diameter = 6
  invert = false
  matchOuter = false
  offset = 0
  thread = false
  type = 7
FEATURE [Part::FeaturePython] Nut010  label="M4-Nut010"  # Fasteners workbench fastener (typed FeaturePython)
  Placement = pos=(23.6881,-43.4871,16) rot=(0,0,1;0rad)
  baseObject = -> b_Clamp_smoth_rod_8mm_single_screw_001_002 [Edge142]
  diameter = 6
  invert = false
  matchOuter = false
  offset = 0
  thread = false
  type = 7
FEATURE [Part::FeaturePython] Nut011  label="M4-Nut011"  # Fasteners workbench fastener (typed FeaturePython)
  Placement = pos=(20.8596,-32.1734,13) rot=(-0.707107,-0.707107,0;1.5708rad)
  baseObject = -> b_Clamp_smoth_rod_8mm_single_screw_001_002 [Edge126]
  diameter = 6
  invert = false
  matchOuter = false
  offset = 0
  thread = false
  type = 7
FEATURE [Part::FeaturePython] Nut012  label="M4-Nut058"  # Fasteners workbench fastener (typed FeaturePython)
  Placement = pos=(-43.4871,23.688,340) rot=(0.945882,0.324511,0;3.14159rad)
  baseObject = -> b_Clamp_smoth_rod_8mm_single_screw_001_007 [Edge169]
  diameter = 6
  invert = true
  matchOuter = false
  offset = 0
  thread = false
  type = 7
FEATURE [Part::FeaturePython] Nut013  label="M4-Nut060"  # Fasteners workbench fastener (typed FeaturePython)
  Placement = pos=(-20.8597,32.1733,343) rot=(0.707106,0.707107,0;1.5708rad)
  baseObject = -> b_Clamp_smoth_rod_8mm_single_screw_001_007 [Edge126]
  diameter = 6
  invert = false
  matchOuter = false
  offset = 0
  thread = false
  type = 7
FEATURE [Part::FeaturePython] Nut014  label="M4-Nut059"  # Fasteners workbench fastener (typed FeaturePython)
  Placement = pos=(-23.6881,43.487,340) rot=(0.945882,0.324511,0;3.14159rad)
  baseObject = -> b_Clamp_smoth_rod_8mm_single_screw_001_007 [Edge168]
  diameter = 6
  invert = true
  matchOuter = false
  offset = 0
  thread = false
  type = 7
FEATURE [Part::FeaturePython] Nut015  label="M4-Nut062"  # Fasteners workbench fastener (typed FeaturePython)
  Placement = pos=(43.4871,-23.6881,340) rot=(0.964002,0.265896,0;3.14159rad)
  baseObject = -> b_Clamp_smoth_rod_8mm_single_screw_001_005 [Edge169]
  diameter = 6
  invert = true
  matchOuter = false
  offset = 0
  thread = false
  type = 7
FEATURE [Part::FeaturePython] Nut016  label="M4-Nut061"  # Fasteners workbench fastener (typed FeaturePython)
  Placement = pos=(23.6881,-43.4871,340) rot=(0.964002,0.265896,0;3.14159rad)
  baseObject = -> b_Clamp_smoth_rod_8mm_single_screw_001_005 [Edge168]
  diameter = 6
  invert = true
  matchOuter = false
  offset = 0
  thread = false
  type = 7
FEATURE [Part::FeaturePython] Nut017  label="M4-Nut068"  # Fasteners workbench fastener (typed FeaturePython)
  Placement = pos=(20.8597,-32.1734,343) rot=(-0.707107,-0.707107,0;1.5708rad)
  baseObject = -> b_Clamp_smoth_rod_8mm_single_screw_001_005 [Edge126]
  diameter = 6
  invert = false
  matchOuter = false
  offset = 0
  thread = false
  type = 7
FEATURE [Part::FeaturePython] Nut018  label="M4-Nut027"  # Fasteners workbench fastener (typed FeaturePython)
  Placement = pos=(43.4871,23.6881,16) rot=(0,0,1;0rad)
  baseObject = -> b_Clamp_smoth_rod_8mm_single_screw_001_001 [Edge169]
  diameter = 6
  invert = true
  matchOuter = false
  offset = 0
  thread = false
  type = 7
FEATURE [Part::FeaturePython] Nut019  label="M4-Nut026"  # Fasteners workbench fastener (typed FeaturePython)
  Placement = pos=(23.6881,43.4871,16) rot=(0,0,1;0rad)
  baseObject = -> b_Clamp_smoth_rod_8mm_single_screw_001_001 [Edge168]
  diameter = 6
  invert = true
  matchOuter = false
  offset = 0
  thread = false
  type = 7
FEATURE [Part::FeaturePython] Nut020  label="M4-Nut022"  # Fasteners workbench fastener (typed FeaturePython)
  Placement = pos=(20.8597,32.1734,13) rot=(0.707107,-0.707107,0;1.5708rad)
  baseObject = -> b_Clamp_smoth_rod_8mm_single_screw_001_001 [Edge126]
  diameter = 6
  invert = false
  matchOuter = false
  offset = 0
  thread = false
  type = 7
FEATURE [Part::FeaturePython] Nut021  label="M4-Nut023"  # Fasteners workbench fastener (typed FeaturePython)
  Placement = pos=(-20.8596,32.1734,13) rot=(0.707107,0.707107,0;1.5708rad)
  baseObject = -> b_Clamp_smoth_rod_8mm_single_screw_001_003 [Edge126]
  diameter = 6
  invert = false
  matchOuter = false
  offset = 0
  thread = false
  type = 7
FEATURE [Part::FeaturePython] Nut022  label="M4-Nut024"  # Fasteners workbench fastener (typed FeaturePython)
  Placement = pos=(-43.4871,23.6881,16) rot=(0,0,1;0rad)
  baseObject = -> b_Clamp_smoth_rod_8mm_single_screw_001_003 [Edge143]
  diameter = 6
  invert = false
  matchOuter = false
  offset = 0
  thread = false
  type = 7
FEATURE [Part::FeaturePython] Nut023  label="M4-Nut025"  # Fasteners workbench fastener (typed FeaturePython)
  Placement = pos=(-23.6881,43.4871,16) rot=(0,0,1;0rad)
  baseObject = -> b_Clamp_smoth_rod_8mm_single_screw_001_003 [Edge142]
  diameter = 6
  invert = false
  matchOuter = false
  offset = 0
  thread = false
  type = 7
FEATURE [Part::FeaturePython] Nut024  label="M3-Nut"  # Fasteners workbench fastener (typed FeaturePython)
  Placement = pos=(-29.5,8,-2) rot=(0.793167,0.609004,0;3.14159rad)
  baseObject = -> b_Z_axis_endstop_support_001_ [Edge61]
  diameter = 4
  invert = true
  matchOuter = false
  offset = 0
  thread = false
  type = 7
FEATURE [Part::FeaturePython] Nut025  label="M3-Nut001"  # Fasteners workbench fastener (typed FeaturePython)
  Placement = pos=(-29.5,-8,-2) rot=(0.793167,0.609004,0;3.14159rad)
  baseObject = -> b_Z_axis_endstop_support_001_ [Edge215]
  diameter = 4
  invert = true
  matchOuter = false
  offset = 0
  thread = false
  type = 7
FEATURE [Part::FeaturePython] Screw  label="M4x20-Screw"  # Fasteners workbench fastener (typed FeaturePython)
  Placement = pos=(23.6881,43.4871,0) rot=(1,0,0;3.14159rad)
  baseObject = -> b_Z_axis_top_plate_001_ [Edge151]
  diameter = 6
  invert = true
  length = 7
  lengthCustom = 20
  matchOuter = false
  offset = 0
  thread = false
  type = 35
FEATURE [Part::FeaturePython] Screw001  label="M4x20-Screw001"  # Fasteners workbench fastener (typed FeaturePython)
  Placement = pos=(-23.6881,43.4871,0) rot=(1,0,0;3.14159rad)
  baseObject = -> b_Z_axis_top_plate_001_ [Edge155]
  diameter = 6
  invert = true
  length = 7
  lengthCustom = 20
  matchOuter = false
  offset = 0
  thread = false
  type = 35
FEATURE [Part::FeaturePython] Screw002  label="M4x20-Screw002"  # Fasteners workbench fastener (typed FeaturePython)
  Placement = pos=(-43.4871,23.6881,0) rot=(1,0,0;3.14159rad)
  baseObject = -> b_Z_axis_top_plate_001_ [Edge143]
  diameter = 6
  invert = true
  length = 7
  lengthCustom = 20
  matchOuter = false
  offset = 0
  thread = false
  type = 35
FEATURE [Part::FeaturePython] Screw003  label="M4x20-Screw003"  # Fasteners workbench fastener (typed FeaturePython)
  Placement = pos=(0,52,0) rot=(1,0,0;3.14159rad)
  baseObject = -> b_Z_axis_top_plate_001_ [Edge147]
  diameter = 6
  invert = true
  length = 7
  lengthCustom = 20
  matchOuter = false
  offset = 0
  thread = false
  type = 35
FEATURE [Part::FeaturePython] Screw004  label="M4x20-Screw004"  # Fasteners workbench fastener (typed FeaturePython)
  Placement = pos=(-23.6881,-43.4871,0) rot=(1,0,0;3.14159rad)
  baseObject = -> b_Z_axis_top_plate_001_ [Edge158]
  diameter = 6
  invert = true
  length = 7
  lengthCustom = 20
  matchOuter = false
  offset = 0
  thread = false
  type = 35
FEATURE [Part::FeaturePython] Screw005  label="M4x20-Screw005"  # Fasteners workbench fastener (typed FeaturePython)
  Placement = pos=(-43.4871,-23.6881,0) rot=(1,0,0;3.14159rad)
  baseObject = -> b_Z_axis_top_plate_001_ [Edge153]
  diameter = 6
  invert = true
  length = 7
  lengthCustom = 20
  matchOuter = false
  offset = 0
  thread = false
  type = 35
FEATURE [Part::FeaturePython] Screw006  label="M4x20-Screw006"  # Fasteners workbench fastener (typed FeaturePython)
  Placement = pos=(0,-52,0) rot=(1,0,0;3.14159rad)
  baseObject = -> b_Z_axis_top_plate_001_ [Edge150]
  diameter = 6
  invert = true
  length = 7
  lengthCustom = 20
  matchOuter = false
  offset = 0
  thread = false
  type = 35
FEATURE [Part::FeaturePython] Screw007  label="M4x20-Screw007"  # Fasteners workbench fastener (typed FeaturePython)
  Placement = pos=(23.6881,-43.4871,0) rot=(1,0,0;3.14159rad)
  baseObject = -> b_Z_axis_top_plate_001_ [Edge159]
  diameter = 6
  invert = true
  length = 7
  lengthCustom = 20
  matchOuter = false
  offset = 0
  thread = false
  type = 35
FEATURE [Part::FeaturePython] Screw008  label="M4x20-Screw008"  # Fasteners workbench fastener (typed FeaturePython)
  Placement = pos=(43.4871,-23.6881,0) rot=(1,0,0;3.14159rad)
  baseObject = -> b_Z_axis_top_plate_001_ [Edge139]
  diameter = 6
  invert = true
  length = 7
  lengthCustom = 20
  matchOuter = false
  offset = 0
  thread = false
  type = 35
FEATURE [Part::FeaturePython] Screw009  label="M4x20-Screw009"  # Fasteners workbench fastener (typed FeaturePython)
  Placement = pos=(43.4871,23.6881,0) rot=(1,0,0;3.14159rad)
  baseObject = -> b_Z_axis_top_plate_001_ [Edge146]
  diameter = 6
  invert = true
  length = 7
  lengthCustom = 20
  matchOuter = false
  offset = 0
  thread = false
  type = 35
FEATURE [Part::FeaturePython] Screw010  label="M3x10-Screw"  # Fasteners workbench fastener (typed FeaturePython)
  Placement = pos=(17.5,15.5,6) rot=(0,0,1;0rad)
  baseObject = -> b_Z_axis_top_plate_001_ [Edge44]
  diameter = 4
  invert = false
  length = 4
  lengthCustom = 10
  matchOuter = false
  offset = 0
  thread = false
  type = 34
FEATURE [Part::FeaturePython] Screw011  label="M3x10-Screw001"  # Fasteners workbench fastener (typed FeaturePython)
  Placement = pos=(48.5,15.5,6) rot=(0,0,1;0rad)
  baseObject = -> b_Z_axis_top_plate_001_ [Edge39]
  diameter = 4
  invert = false
  length = 4
  lengthCustom = 10
  matchOuter = false
  offset = 0
  thread = false
  type = 34
FEATURE [Part::FeaturePython] Screw012  label="M3x10-Screw002"  # Fasteners workbench fastener (typed FeaturePython)
  Placement = pos=(17.5,-15.5,6) rot=(0,0,1;0rad)
  baseObject = -> b_Z_axis_top_plate_001_ [Edge43]
  diameter = 4
  invert = false
  length = 4
  lengthCustom = 10
  matchOuter = false
  offset = 0
  thread = false
  type = 34
FEATURE [Part::FeaturePython] Screw013  label="M3x10-Screw003"  # Fasteners workbench fastener (typed FeaturePython)
  Placement = pos=(48.5,-15.5,6) rot=(0,0,1;0rad)
  baseObject = -> b_Z_axis_top_plate_001_ [Edge40]
  diameter = 4
  invert = false
  length = 4
  lengthCustom = 10
  matchOuter = false
  offset = 0
  thread = false
  type = 34
FEATURE [Part::FeaturePython] Screw014  label="M4x35-Screw"  # Fasteners workbench fastener (typed FeaturePython)
  Placement = pos=(43.4871,-23.6881,368) rot=(0,0,1;0rad)
  baseObject = -> b_J1_coupler_8mm1_001_ [Edge91]
  diameter = 6
  invert = true
  length = 10
  lengthCustom = 35
  matchOuter = false
  offset = 0
  thread = false
  type = 34
FEATURE [Part::FeaturePython] Screw015  label="M4x35-Screw022"  # Fasteners workbench fastener (typed FeaturePython)
  Placement = pos=(23.6881,-43.4871,368) rot=(0,0,1;0rad)
  baseObject = -> b_J1_coupler_8mm1_001_ [Edge191]
  diameter = 6
  invert = true
  length = 10
  lengthCustom = 35
  matchOuter = false
  offset = 0
  thread = false
  type = 34
FEATURE [Part::FeaturePython] Screw016  label="M4x35-Screw021"  # Fasteners workbench fastener (typed FeaturePython)
  Placement = pos=(-23.688,-43.4871,368) rot=(0,0,1;0rad)
  baseObject = -> b_J1_coupler_8mm1_001_ [Edge198]
  diameter = 6
  invert = true
  length = 10
  lengthCustom = 35
  matchOuter = false
  offset = 0
  thread = false
  type = 34
FEATURE [Part::FeaturePython] Screw017  label="M4x35-Screw020"  # Fasteners workbench fastener (typed FeaturePython)
  Placement = pos=(-43.487,-23.6881,368) rot=(0,0,1;0rad)
  baseObject = -> b_J1_coupler_8mm1_001_ [Edge197]
  diameter = 6
  invert = true
  length = 10
  lengthCustom = 35
  matchOuter = false
  offset = 0
  thread = false
  type = 34
FEATURE [Part::FeaturePython] Screw018  label="M4x35-Screw019"  # Fasteners workbench fastener (typed FeaturePython)
  Placement = pos=(-43.4871,23.688,368) rot=(0,0,1;0rad)
  baseObject = -> b_J1_coupler_8mm1_001_ [Edge193]
  diameter = 6
  invert = true
  length = 10
  lengthCustom = 35
  matchOuter = false
  offset = 0
  thread = false
  type = 34
FEATURE [Part::FeaturePython] Screw019  label="M4x35-Screw017"  # Fasteners workbench fastener (typed FeaturePython)
  Placement = pos=(23.6881,43.4871,368) rot=(0,0,1;0rad)
  baseObject = -> b_J1_coupler_8mm1_001_ [Edge187]
  diameter = 6
  invert = true
  length = 10
  lengthCustom = 35
  matchOuter = false
  offset = 0
  thread = false
  type = 34
FEATURE [Part::FeaturePython] Screw020  label="M4x35-Screw023"  # Fasteners workbench fastener (typed FeaturePython)
  Placement = pos=(43.4871,23.6881,368) rot=(0,0,1;0rad)
  baseObject = -> b_J1_coupler_8mm1_001_ [Edge83]
  diameter = 6
  invert = true
  length = 10
  lengthCustom = 35
  matchOuter = false
  offset = 0
  thread = false
  type = 34
FEATURE [Part::FeaturePython] Screw021  label="M4x35-Screw018"  # Fasteners workbench fastener (typed FeaturePython)
  Placement = pos=(-23.6881,43.487,368) rot=(0,0,1;0rad)
  baseObject = -> b_J1_coupler_8mm1_001_ [Edge194]
  diameter = 6
  invert = true
  length = 10
  lengthCustom = 35
  matchOuter = false
  offset = 0
  thread = false
  type = 34
FEATURE [Part::FeaturePython] Screw022  label="M4x20-Screw027"  # Fasteners workbench fastener (typed FeaturePython)
  Placement = pos=(30.4056,41.7193,343) rot=(-0.707107,0.707107,0;1.5708rad)
  baseObject = -> b_Clamp_smoth_rod_8mm_single_screw_001_004 [Edge125]
  diameter = 6
  invert = true
  length = 7
  lengthCustom = 20
  matchOuter = false
  offset = 0
  thread = false
  type = 34
FEATURE [Part::FeaturePython] Screw023  label="M4x20-Screw026"  # Fasteners workbench fastener (typed FeaturePython)
  Placement = pos=(30.4056,-41.7193,343) rot=(0.707107,0.707107,0;1.5708rad)
  baseObject = -> b_Clamp_smoth_rod_8mm_single_screw_001_005 [Edge125]
  diameter = 6
  invert = true
  length = 7
  lengthCustom = 20
  matchOuter = false
  offset = 0
  thread = false
  type = 34
FEATURE [Part::FeaturePython] Screw024  label="M4x20-Screw024"  # Fasteners workbench fastener (typed FeaturePython)
  Placement = pos=(-30.4055,-41.7194,343) rot=(0.707106,-0.707107,0;1.5708rad)
  baseObject = -> b_Clamp_smoth_rod_8mm_single_screw_001_006 [Edge125]
  diameter = 6
  invert = true
  length = 7
  lengthCustom = 20
  matchOuter = false
  offset = 0
  thread = false
  type = 34
FEATURE [Part::FeaturePython] Screw025  label="M4x20-Screw025"  # Fasteners workbench fastener (typed FeaturePython)
  Placement = pos=(-30.4056,41.7193,343) rot=(-0.707106,-0.707107,0;1.5708rad)
  baseObject = -> b_Clamp_smoth_rod_8mm_single_screw_001_007 [Edge125]
  diameter = 6
  invert = true
  length = 7
  lengthCustom = 20
  matchOuter = false
  offset = 0
  thread = false
  type = 34
FEATURE [Part::FeaturePython] Screw026  label="M4x20-Screw014"  # Fasteners workbench fastener (typed FeaturePython)
  Placement = pos=(-30.4056,41.7193,13) rot=(-0.707107,-0.707107,0;1.5708rad)
  baseObject = -> b_Clamp_smoth_rod_8mm_single_screw_001_003 [Edge125]
  diameter = 6
  invert = true
  length = 7
  lengthCustom = 20
  matchOuter = false
  offset = 0
  thread = false
  type = 34
FEATURE [Part::FeaturePython] Screw027  label="M4x20-Screw015"  # Fasteners workbench fastener (typed FeaturePython)
  Placement = pos=(30.4056,41.7193,13) rot=(-0.707107,0.707107,0;1.5708rad)
  baseObject = -> b_Clamp_smoth_rod_8mm_single_screw_001_001 [Edge125]
  diameter = 6
  invert = true
  length = 7
  lengthCustom = 20
  matchOuter = false
  offset = 0
  thread = false
  type = 34
FEATURE [Part::FeaturePython] Screw028  label="M4x20-Screw016"  # Fasteners workbench fastener (typed FeaturePython)
  Placement = pos=(30.4056,-41.7193,13) rot=(0.707107,0.707107,0;1.5708rad)
  baseObject = -> b_Clamp_smoth_rod_8mm_single_screw_001_002 [Edge125]
  diameter = 6
  invert = true
  length = 7
  lengthCustom = 20
  matchOuter = false
  offset = 0
  thread = false
  type = 34
FEATURE [Part::FeaturePython] Screw029  label="M4x20-Screw017"  # Fasteners workbench fastener (typed FeaturePython)
  Placement = pos=(-30.4056,-41.7193,13) rot=(0.707107,-0.707107,0;1.5708rad)
  baseObject = -> b_Clamp_smoth_rod_8mm_single_screw_001_ [Edge125]
  diameter = 6
  invert = true
  length = 7
  lengthCustom = 20
  matchOuter = false
  offset = 0
  thread = false
  type = 34
FEATURE [Part::FeaturePython] Screw030  label="M4x35-Screw024"  # Fasteners workbench fastener (typed FeaturePython)
  Placement = pos=(49.52,1.18237e-05,368) rot=(0,0,1;0rad)
  baseObject = -> b_J1_coupler_8mm1_001_ [Edge189]
  diameter = 6
  invert = true
  length = 10
  lengthCustom = 35
  matchOuter = false
  offset = 0
  thread = false
  type = 34
FEATURE [Part::FeaturePython] Screw031  label="M4x25-Screw"  # Fasteners workbench fastener (typed FeaturePython)
  Placement = pos=(6.18516e-05,-49.52,368) rot=(0,0,1;0rad)
  baseObject = -> b_J1_coupler_8mm1_001_ [Edge192]
  diameter = 6
  invert = true
  length = 8
  lengthCustom = 25
  matchOuter = false
  offset = 0
  thread = false
  type = 34
FEATURE [Part::FeaturePython] Screw032  label="M4x25-Screw005"  # Fasteners workbench fastener (typed FeaturePython)
  Placement = pos=(-49.52,-6.18896e-05,368) rot=(0,0,1;0rad)
  baseObject = -> b_J1_coupler_8mm1_001_ [Edge196]
  diameter = 6
  invert = true
  length = 8
  lengthCustom = 25
  matchOuter = false
  offset = 0
  thread = false
  type = 34
FEATURE [Part::FeaturePython] Screw033  label="M4x25-Screw004"  # Fasteners workbench fastener (typed FeaturePython)
  Placement = pos=(-1.18618e-05,49.52,368) rot=(0,0,1;0rad)
  baseObject = -> b_J1_coupler_8mm1_001_ [Edge195]
  diameter = 6
  invert = true
  length = 8
  lengthCustom = 25
  matchOuter = false
  offset = 0
  thread = false
  type = 34
FEATURE [Part::FeaturePython] Nut026  label="M4-Nut034"  # Fasteners workbench fastener (typed FeaturePython)
  Placement = pos=(6.73165e-05,-49.52,350) rot=(0.984704,0.174236,0;3.14159rad)
  baseObject = -> b_Z_axis_bottom_plate_001_ [Edge109]
  diameter = 2
  invert = false
  matchOuter = false
  offset = 0
  thread = false
  type = 5
FEATURE [Part::FeaturePython] Nut027  label="M4-Nut035"  # Fasteners workbench fastener (typed FeaturePython)
  Placement = pos=(-49.52,-6.2943e-05,350) rot=(0.984704,0.174236,0;3.14159rad)
  baseObject = -> b_Z_axis_bottom_plate_001_ [Edge113]
  diameter = 2
  invert = false
  matchOuter = false
  offset = 0
  thread = false
  type = 5
FEATURE [Part::FeaturePython] Nut028  label="M4-Nut036"  # Fasteners workbench fastener (typed FeaturePython)
  Placement = pos=(-1.75911e-05,49.52,350) rot=(0.984704,0.174236,0;3.14159rad)
  baseObject = -> b_Z_axis_bottom_plate_001_ [Edge118]
  diameter = 2
  invert = false
  matchOuter = false
  offset = 0
  thread = false
  type = 5
FEATURE [Part::FeaturePython] Nut029  label="M4-Nut063"  # Fasteners workbench fastener (typed FeaturePython)
  Placement = pos=(49.52,1.62409e-05,342.5) rot=(0.901759,0.432239,0;3.14159rad)
  baseObject = -> b_Bearing_608_spacer_001_ [Edge134]
  diameter = 6
  invert = true
  matchOuter = false
  offset = 0
  thread = false
  type = 7
FEATURE [Part::FeaturePython] Nut030  label="M4-Nut066"  # Fasteners workbench fastener (typed FeaturePython)
  Placement = pos=(24.74,14.3067,342.5) rot=(0.901759,0.432239,0;3.14159rad)
  baseObject = -> b_Bearing_608_spacer_001_ [Edge132]
  diameter = 6
  invert = true
  matchOuter = false
  offset = 0
  thread = false
  type = 7
FEATURE [Part::FeaturePython] Nut031  label="M4-Nut067"  # Fasteners workbench fastener (typed FeaturePython)
  Placement = pos=(24.74,-14.3067,342.5) rot=(0.901759,0.432239,0;3.14159rad)
  baseObject = -> b_Bearing_608_spacer_001_ [Edge130]
  diameter = 6
  invert = true
  matchOuter = false
  offset = 0
  thread = false
  type = 7
FEATURE [Part::FeaturePython] Screw034  label="M4x20-Screw018"  # Fasteners workbench fastener (typed FeaturePython)
  Placement = pos=(24.74,-14.3067,360) rot=(0.984704,0.174236,0;0rad)
  baseObject = -> b_Z_axis_bottom_plate_001_ [Edge1]
  diameter = 6
  invert = true
  length = 7
  lengthCustom = 20
  matchOuter = false
  offset = 0
  thread = false
  type = 35
FEATURE [Part::FeaturePython] Screw035  label="M4x20-Screw019"  # Fasteners workbench fastener (typed FeaturePython)
  Placement = pos=(24.74,14.3067,360) rot=(0.984704,0.174236,0;0rad)
  baseObject = -> b_Z_axis_bottom_plate_001_ [Edge40]
  diameter = 6
  invert = true
  length = 7
  lengthCustom = 20
  matchOuter = false
  offset = 0
  thread = false
  type = 35
FEATURE [Part::FeaturePython] Screw036  label="M4x60-Screw"  # Fasteners workbench fastener (typed FeaturePython)
  Placement = pos=(12.5,-1.5594e-05,360) rot=(0.997982,0.063491,0;3.14159rad)
  baseObject = -> b_J1_coupler_8mm1_001_ [Edge2]
  diameter = 6
  invert = false
  length = 12
  lengthCustom = 60
  matchOuter = false
  offset = 0
  thread = false
  type = 35
FEATURE [Part::FeaturePython] Screw037  label="M4x60-Screw007"  # Fasteners workbench fastener (typed FeaturePython)
  Placement = pos=(3.42898e-05,-12.5,360) rot=(0.997982,0.063491,0;3.14159rad)
  baseObject = -> b_J1_coupler_8mm1_001_ [Edge23]
  diameter = 6
  invert = false
  length = 12
  lengthCustom = 60
  matchOuter = false
  offset = 0
  thread = false
  type = 35
FEATURE [Part::FeaturePython] Screw038  label="M4x60-Screw009"  # Fasteners workbench fastener (typed FeaturePython)
  Placement = pos=(1.56828e-05,12.5,360) rot=(0.997982,0.063491,0;3.14159rad)
  baseObject = -> b_J1_coupler_8mm1_001_ [Edge9]
  diameter = 6
  invert = false
  length = 12
  lengthCustom = 60
  matchOuter = false
  offset = 0
  thread = false
  type = 35
FEATURE [Part::FeaturePython] Screw039  label="M4x60-Screw008"  # Fasteners workbench fastener (typed FeaturePython)
  Placement = pos=(-12.5,-3.4201e-05,360) rot=(0.997982,0.063491,0;3.14159rad)
  baseObject = -> b_J1_coupler_8mm1_001_ [Edge16]
  diameter = 6
  invert = false
  length = 12
  lengthCustom = 60
  matchOuter = false
  offset = 0
  thread = false
  type = 35
FEATURE [Part::FeaturePython] b_Thrust_bearing_511081_001_  label="Thrust_bearing_511081_001"  # a2plus imported part (geometry in sourceFile) (typed FeaturePython)
  Placement = pos=(2.50112e-05,-2.55444e-05,381) rot=(-1,0,0;1.5708rad)
  a2p_Version = V0.1
  fixedPosition = false
  objectType = a2pPart
  sourceFile = ./Thrust_bearing_51108.step
  subassemblyImport = false
  timeLastImport = 1.61989e+09
  updateColors = true
FEATURE [App::FeaturePython] circularEdge_010  label="circularEdge_010__Thrust_bearing_511081_001"  # a2plus constraint (typed FeaturePython)
  Object1 = b_J1_coupler_8mm1_001_
  Object2 = b_Thrust_bearing_511081_001_
  ParentTreeObject = -> b_J1_coupler_8mm1_001_
  SubElement1 = Edge47
  SubElement2 = Edge21
  Suppressed = false
  Type = circularEdge
  directionConstraint = 1
  lockRotation = false
  offset = 0
FEATURE [App::FeaturePython] circularEdge_010_mirror  label="circularEdge_010__J1_coupler_8mm1_001"  # a2plus constraint (typed FeaturePython)
  Object1 = b_J1_coupler_8mm1_001_
  Object2 = b_Thrust_bearing_511081_001_
  ParentTreeObject = -> b_Thrust_bearing_511081_001_
  SubElement1 = Edge47
  SubElement2 = Edge21
  Suppressed = false
  Type = circularEdge
  directionConstraint = 1
  lockRotation = false
  offset = 0
FEATURE [Part::FeaturePython] Nut032  label="M4-Nut041"  # Fasteners workbench fastener (typed FeaturePython)
  Placement = pos=(-1.1981e-06,-52,13.4) rot=(0,0,1;0rad)
  baseObject = -> b_Top_cover_8mm_001_ [Edge7]
  diameter = 6
  invert = true
  matchOuter = false
  offset = 0
  thread = false
  type = 7
FEATURE [Part::FeaturePython] Nut033  label="M4-Nut042"  # Fasteners workbench fastener (typed FeaturePython)
  Placement = pos=(1.08305e-06,52,13.4) rot=(0,0,1;0rad)
  baseObject = -> b_Top_cover_8mm_001_ [Edge126]
  diameter = 6
  invert = true
  matchOuter = false
  offset = 0
  thread = false
  type = 7
FEATURE [Part::FeaturePython] Screw040  label="M3x12-Screw"  # Fasteners workbench fastener (typed FeaturePython)
  Placement = pos=(-29.5,8,6) rot=(0,0,1;0rad)
  baseObject = -> b_Z_axis_top_plate_001_ [Edge46]
  diameter = 4
  invert = false
  length = 5
  lengthCustom = 12
  matchOuter = false
  offset = 0
  thread = false
  type = 35
FEATURE [Part::FeaturePython] Screw041  label="M3x12-Screw001"  # Fasteners workbench fastener (typed FeaturePython)
  Placement = pos=(-29.5,-8,6) rot=(0,0,1;0rad)
  baseObject = -> b_Z_axis_top_plate_001_ [Edge9]
  diameter = 4
  invert = false
  length = 5
  lengthCustom = 12
  matchOuter = false
  offset = 0
  thread = false
  type = 35
FEATURE [Part::FeaturePython] b_Flexible_coupling__5_8mm1_001_  label="Flexible_coupling_ 5-8mm1_001"  # a2plus imported part (geometry in sourceFile) (typed FeaturePython)
  Placement = pos=(33,1.0074e-08,2.49) rot=(1,0,0;1.5708rad)
  a2p_Version = V0.1
  fixedPosition = false
  objectType = a2pPart
  sourceFile = ./Flexible_coupling_ 5-8mm.step
  subassemblyImport = false
  timeLastImport = 1.62009e+09
  updateColors = true
FEATURE [App::FeaturePython] circularEdge_011  label="circularEdge_011__Stepper NEMA 17 -  20mm shaft1_001"  # a2plus constraint (typed FeaturePython)
  Object1 = b_Flexible_coupling__5_8mm1_001_
  Object2 = b_Stepper_NEMA_17____20mm_shaft1_001_
  ParentTreeObject = -> b_Flexible_coupling__5_8mm1_001_
  SubElement1 = Edge67
  SubElement2 = Edge57
  Suppressed = false
  Type = circularEdge
  directionConstraint = 1
  lockRotation = false
  offset = 0.5
FEATURE [App::FeaturePython] circularEdge_011_mirror  label="circularEdge_011__Flexible_coupling_ 5-8mm1_001"  # a2plus constraint (typed FeaturePython)
  Object1 = b_Flexible_coupling__5_8mm1_001_
  Object2 = b_Stepper_NEMA_17____20mm_shaft1_001_
  ParentTreeObject = -> b_Stepper_NEMA_17____20mm_shaft1_001_
  SubElement1 = Edge67
  SubElement2 = Edge57
  Suppressed = false
  Type = circularEdge
  directionConstraint = 1
  lockRotation = false
  offset = 0.5
FEATURE [App::FeaturePython] axisCoincident_015  label="axisCoincident_015__J1_coupler_8mm1_001"  # a2plus constraint (typed FeaturePython)
  Object1 = b_Z_axis_bottom_plate_001_
  Object2 = b_J1_coupler_8mm1_001_
  ParentTreeObject = -> b_Z_axis_bottom_plate_001_
  SubElement1 = Face4
  SubElement2 = Face11
  Suppressed = false
  Type = axial
  directionConstraint = 0
  lockRotation = false
FEATURE [App::FeaturePython] axisCoincident_015_mirror  label="axisCoincident_015__Z-axis_bottom_plate_001"  # a2plus constraint (typed FeaturePython)
  Object1 = b_Z_axis_bottom_plate_001_
  Object2 = b_J1_coupler_8mm1_001_
  ParentTreeObject = -> b_J1_coupler_8mm1_001_
  SubElement1 = Face4
  SubElement2 = Face11
  Suppressed = false
  Type = axial
  directionConstraint = 0
  lockRotation = false
FEATURE [App::FeaturePython] axisCoincident_016  label="axisCoincident_016__Z-axis_bottom_plate_001"  # a2plus constraint (typed FeaturePython)
  Object1 = b_Base_cover_8mm_001_
  Object2 = b_Z_axis_bottom_plate_001_
  ParentTreeObject = -> b_Base_cover_8mm_001_
  SubElement1 = Face14
  SubElement2 = Face3
  Suppressed = false
  Type = axial
  directionConstraint = 1
  lockRotation = false
FEATURE [App::FeaturePython] axisCoincident_016_mirror  label="axisCoincident_016__Base_cover_8mm_001"  # a2plus constraint (typed FeaturePython)
  Object1 = b_Base_cover_8mm_001_
  Object2 = b_Z_axis_bottom_plate_001_
  ParentTreeObject = -> b_Z_axis_bottom_plate_001_
  SubElement1 = Face14
  SubElement2 = Face3
  Suppressed = false
  Type = axial
  directionConstraint = 1
  lockRotation = false
FEATURE [App::FeaturePython] planeCoincident_008  label="planeCoincident_008__Z-axis_bottom_plate_001"  # a2plus constraint (typed FeaturePython)
  Object1 = b_Base_cover_8mm_001_
  Object2 = b_Z_axis_bottom_plate_001_
  ParentTreeObject = -> b_Base_cover_8mm_001_
  SubElement1 = Face16
  SubElement2 = Face24
  Suppressed = false
  Type = plane
  directionConstraint = 1
  offset = 0
FEATURE [App::FeaturePython] planeCoincident_008_mirror  label="planeCoincident_008__Base_cover_8mm_001"  # a2plus constraint (typed FeaturePython)
  Object1 = b_Base_cover_8mm_001_
  Object2 = b_Z_axis_bottom_plate_001_
  ParentTreeObject = -> b_Z_axis_bottom_plate_001_
  SubElement1 = Face16
  SubElement2 = Face24
  Suppressed = false
  Type = plane
  directionConstraint = 1
  offset = 0
FEATURE [App::FeaturePython] planeCoincident_009  label="planeCoincident_009__Z-axis_bottom_plate_001"  # a2plus constraint (typed FeaturePython)
  Object1 = b_J1_coupler_8mm1_001_
  Object2 = b_Z_axis_bottom_plate_001_
  ParentTreeObject = -> b_J1_coupler_8mm1_001_
  SubElement1 = Face39
  SubElement2 = Face1
  Suppressed = false
  Type = plane
  directionConstraint = 0
  offset = 0
FEATURE [App::FeaturePython] planeCoincident_009_mirror  label="planeCoincident_009__J1_coupler_8mm1_001"  # a2plus constraint (typed FeaturePython)
  Object1 = b_J1_coupler_8mm1_001_
  Object2 = b_Z_axis_bottom_plate_001_
  ParentTreeObject = -> b_Z_axis_bottom_plate_001_
  SubElement1 = Face39
  SubElement2 = Face1
  Suppressed = false
  Type = plane
  directionConstraint = 0
  offset = 0
FEATURE [App::FeaturePython] circularEdge_008  label="circularEdge_008__Bearing_608_spacer_001"  # a2plus constraint (typed FeaturePython)
  Object1 = b_Z_axis_bottom_plate_001_
  Object2 = b_Bearing_608_spacer_001_
  ParentTreeObject = -> b_Z_axis_bottom_plate_001_
  SubElement1 = Edge67
  SubElement2 = Edge10
  Suppressed = false
  Type = circularEdge
  directionConstraint = 0
  lockRotation = false
  offset = 0
FEATURE [App::FeaturePython] circularEdge_008_mirror  label="circularEdge_008__Z-axis_bottom_plate_001"  # a2plus constraint (typed FeaturePython)
  Object1 = b_Z_axis_bottom_plate_001_
  Object2 = b_Bearing_608_spacer_001_
  ParentTreeObject = -> b_Bearing_608_spacer_001_
  SubElement1 = Edge67
  SubElement2 = Edge10
  Suppressed = false
  Type = circularEdge
  directionConstraint = 0
  lockRotation = false
  offset = 0
FEATURE [App::FeaturePython] axisCoincident_017  label="axisCoincident_017__Z-axis_bottom_plate_001"  # a2plus constraint (typed FeaturePython)
  Object1 = b_Bearing_608_spacer_001_
  Object2 = b_Z_axis_bottom_plate_001_
  ParentTreeObject = -> b_Bearing_608_spacer_001_
  SubElement1 = Face50
  SubElement2 = Face18
  Suppressed = false
  Type = axial
  directionConstraint = 0
  lockRotation = false
FEATURE [App::FeaturePython] axisCoincident_017_mirror  label="axisCoincident_017__Bearing_608_spacer_001"  # a2plus constraint (typed FeaturePython)
  Object1 = b_Bearing_608_spacer_001_
  Object2 = b_Z_axis_bottom_plate_001_
  ParentTreeObject = -> b_Z_axis_bottom_plate_001_
  SubElement1 = Face50
  SubElement2 = Face18
  Suppressed = false
  Type = axial
  directionConstraint = 0
  lockRotation = false
FEATURE [App::FeaturePython] circularEdge_012  label="circularEdge_012__Z-axis_bottom_plate_001"  # a2plus constraint (typed FeaturePython)
  Object1 = b_Clamp_smoth_rod_8mm_single_screw_001_007
  Object2 = b_Z_axis_bottom_plate_001_
  ParentTreeObject = -> b_Clamp_smoth_rod_8mm_single_screw_001_007
  SubElement1 = Edge4
  SubElement2 = Edge33
  Suppressed = false
  Type = circularEdge
  directionConstraint = 0
  lockRotation = false
  offset = 0
FEATURE [App::FeaturePython] circularEdge_012_mirror  label="circularEdge_012__Clamp_smoth_rod_8mm_single_screw_008"  # a2plus constraint (typed FeaturePython)
  Object1 = b_Clamp_smoth_rod_8mm_single_screw_001_007
  Object2 = b_Z_axis_bottom_plate_001_
  ParentTreeObject = -> b_Z_axis_bottom_plate_001_
  SubElement1 = Edge4
  SubElement2 = Edge33
  Suppressed = false
  Type = circularEdge
  directionConstraint = 0
  lockRotation = false
  offset = 0
FEATURE [App::FeaturePython] axisCoincident_018  label="axisCoincident_018__Clamp_smoth_rod_8mm_single_screw_007"  # a2plus constraint (typed FeaturePython)
  Object1 = b_Z_axis_bottom_plate_001_
  Object2 = b_Clamp_smoth_rod_8mm_single_screw_001_006
  ParentTreeObject = -> b_Z_axis_bottom_plate_001_
  SubElement1 = Face6
  SubElement2 = Face5
  Suppressed = false
  Type = axial
  directionConstraint = 1
  lockRotation = false
FEATURE [App::FeaturePython] axisCoincident_018_mirror  label="axisCoincident_018__Z-axis_bottom_plate_001"  # a2plus constraint (typed FeaturePython)
  Object1 = b_Z_axis_bottom_plate_001_
  Object2 = b_Clamp_smoth_rod_8mm_single_screw_001_006
  ParentTreeObject = -> b_Clamp_smoth_rod_8mm_single_screw_001_006
  SubElement1 = Face6
  SubElement2 = Face5
  Suppressed = false
  Type = axial
  directionConstraint = 1
  lockRotation = false
FEATURE [App::FeaturePython] axisCoincident_019  label="axisCoincident_019__Clamp_smoth_rod_8mm_single_screw_006"  # a2plus constraint (typed FeaturePython)
  Object1 = b_Z_axis_bottom_plate_001_
  Object2 = b_Clamp_smoth_rod_8mm_single_screw_001_005
  ParentTreeObject = -> b_Z_axis_bottom_plate_001_
  SubElement1 = Face9
  SubElement2 = Face5
  Suppressed = false
  Type = axial
  directionConstraint = 0
  lockRotation = false
FEATURE [App::FeaturePython] axisCoincident_019_mirror  label="axisCoincident_019__Z-axis_bottom_plate_001"  # a2plus constraint (typed FeaturePython)
  Object1 = b_Z_axis_bottom_plate_001_
  Object2 = b_Clamp_smoth_rod_8mm_single_screw_001_005
  ParentTreeObject = -> b_Clamp_smoth_rod_8mm_single_screw_001_005
  SubElement1 = Face9
  SubElement2 = Face5
  Suppressed = false
  Type = axial
  directionConstraint = 0
  lockRotation = false
FEATURE [App::FeaturePython] axisCoincident_020  label="axisCoincident_020__Clamp_smoth_rod_8mm_single_screw_005"  # a2plus constraint (typed FeaturePython)
  Object1 = b_Z_axis_bottom_plate_001_
  Object2 = b_Clamp_smoth_rod_8mm_single_screw_001_004
  ParentTreeObject = -> b_Z_axis_bottom_plate_001_
  SubElement1 = Face8
  SubElement2 = Face5
  Suppressed = false
  Type = axial
  directionConstraint = 1
  lockRotation = false
FEATURE [App::FeaturePython] axisCoincident_020_mirror  label="axisCoincident_020__Z-axis_bottom_plate_001"  # a2plus constraint (typed FeaturePython)
  Object1 = b_Z_axis_bottom_plate_001_
  Object2 = b_Clamp_smoth_rod_8mm_single_screw_001_004
  ParentTreeObject = -> b_Clamp_smoth_rod_8mm_single_screw_001_004
  SubElement1 = Face8
  SubElement2 = Face5
  Suppressed = false
  Type = axial
  directionConstraint = 1
  lockRotation = false
FEATURE [Spreadsheet::Sheet] Fasteners_BOM
  cells = A1=Type; B1=Qty; A2=DIN985 Nut M4; B2=3; A3=ISO4032 Nut M3; B3=2; A4=ISO4032 Nut M4; B4=29; A5=ISO7045 Screw M3x10; B5=4; A6=ISO7045 Screw M4x20; B6=8; A7=ISO7045 Screw M4x25; B7=3; A8=ISO7045 Screw M4x35; B8=9; A9=ISO7046 Screw M3x12; B9=2; A10=ISO7046 Screw M4x20; B10=12; A11=ISO7046 Screw M4x60; B11=4
FEATURE [Spreadsheet::Sheet] _PARTSLIST_  label="#PARTSLIST#"
  cells = A1=POS; B1=QTY; C1=IDENTNO; D1=DESCRIPTION; E1=SUPPLIER; F1=SUPP.IDENTNO; G1=SUPP.DESCRIPTION; H1=(FILENAME); A2=1; B2=1; C2=*; D2=*; E2=*; F2=*; G2=*; H2=Z-axis_top_plate.FCStd; A3=2; B3=8; C3=*; D3=*; E3=*; F3=*; G3=*; H3=Clamp_smoth_rod_8mm_single_screw.FCStd; A4=3; B4=1; C4=*; D4=*; E4=*; F4=*; G4=*; H4=Top_cover_8mm.FCStd; A5=4; B5=1; C5=*; D5=*; E5=*; F5=*; G5=*; H5=Z-axis_endstop_support.FCStd; A6=5; B6=1; C6=*; D6=*; E6=*; F6=*; G6=*; H6=Stepper NEMA 17 -  20mm shaft.step; A7=6; B7=1; C7=*; D7=*; E7=*; F7=*; G7=*; H7=Micro switch.step; A8=7; B8=2; C8=*; D8=*; E8=*; F8=*; G8=*; H8=pin_3mmx10mm.FCStd; A9=8; B9=1; C9=*; D9=*; E9=*; F9=*; G9=*; H9=TR8_lead_screw_300mm.FCStd; A10=9; B10=1; C10=*; D10=*; E10=*; F10=*; G10=*; H10=Z-axis_bottom_plate.FCStd; A11=10; B11=1; C11=*; D11=*; E11=*; F11=*; G11=*; H11=Bearing_608_spacer.FCStd; A12=11; B12=1; C12=*; D12=*; E12=*; F12=*; G12=*; H12=Ball_bearing_608.step; A13=12; B13=1; C13=*; D13=*; E13=*; F13=*; G13=*; H13=J1_coupler_8mm.step; A14=13; B14=1; C14=*; D14=*; E14=*; F14=*; G14=*; H14=Base_cover_8mm.FCStd; A15=14; B15=4; C15=*; D15=*; E15=*; F15=*; G15=*; H15=Smooth_rod_8mm_360mm.FCStd; A16=15; B16=1; C16=*; D16=*; E16=*; F16=*; G16=*; H16=Thrust_bearing_51108.step; A17=16; B17=1; C17=*; D17=*; E17=*; F17=*; G17=*; H17=Flexible_coupling_ 5-8mm.step
